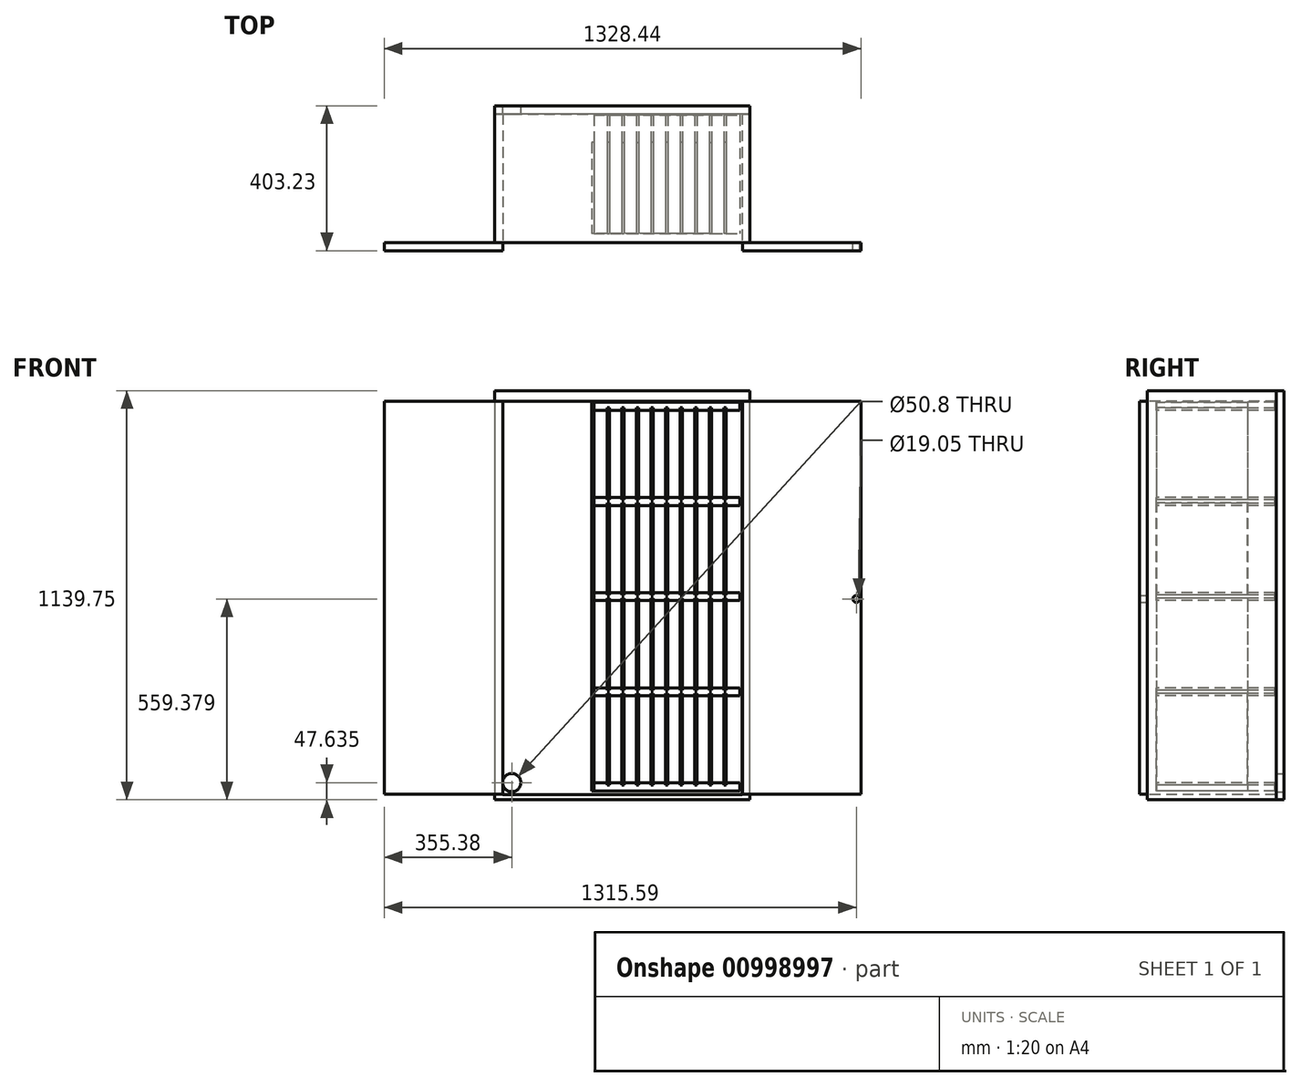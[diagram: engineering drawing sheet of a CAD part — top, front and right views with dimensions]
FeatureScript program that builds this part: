
annotation { "Feature Type Name" : "Feature", "Feature Type Description" : "" }
export const myFeature = defineFeature(function(context is Context, id is Id, definition is map)
    precondition{}
    {
        {
            var Q0;
            Q0=qCreatedBy(makeId("Front.planeOp"),FACE);
            var sketch = newSketch(context, id + "F0", { "sketchPlane" : qUnion([Q0])});
            skLineSegment(sketch, "E0.left", {"start": v(-203.2, -26.35) * mm, "end": v(-203.2, -4.13) * mm});
            skLineSegment(sketch, "E0.right", {"start": v(203.2, -26.35) * mm, "end": v(203.2, -4.13) * mm});
            skPoint(sketch, "E0.middle", {"position": v(0, -15.24) * mm});
            skLineSegment(sketch, "E1", {"start": v(159.39, -10.48) * mm, "end": v(165.74, -10.48) * mm});
            skLineSegment(sketch, "E2", {"start": v(165.74, -20) * mm, "end": v(159.39, -20) * mm});
            skLineSegment(sketch, "E3", {"start": v(165.74, -26.35) * mm, "end": v(165.74, -20) * mm});
            skLineSegment(sketch, "E4", {"start": v(165.74, -10.48) * mm, "end": v(165.74, -4.13) * mm});
            skLineSegment(sketch, "E5", {"start": v(159.39, -4.13) * mm, "end": v(159.39, -10.48) * mm});
            skLineSegment(sketch, "E6", {"start": v(159.39, -20) * mm, "end": v(159.39, -26.35) * mm});
            skLineSegment(sketch, "E7.1.0.2", {"start": v(118.75, -10.48) * mm, "end": v(125.1, -10.48) * mm});
            skLineSegment(sketch, "E7.1.0.3", {"start": v(118.75, -4.13) * mm, "end": v(118.75, -10.48) * mm});
            skLineSegment(sketch, "E7.1.0.4", {"start": v(125.1, -26.35) * mm, "end": v(125.1, -20) * mm});
            skLineSegment(sketch, "E7.1.0.5", {"start": v(125.1, -10.48) * mm, "end": v(125.1, -4.13) * mm});
            skLineSegment(sketch, "E7.1.0.6", {"start": v(125.1, -20) * mm, "end": v(118.75, -20) * mm});
            skLineSegment(sketch, "E7.1.0.7", {"start": v(118.75, -20) * mm, "end": v(118.75, -26.35) * mm});
            skLineSegment(sketch, "E7.2.0.2", {"start": v(78.1, -10.48) * mm, "end": v(84.46, -10.48) * mm});
            skLineSegment(sketch, "E7.2.0.3", {"start": v(78.1, -4.13) * mm, "end": v(78.1, -10.48) * mm});
            skLineSegment(sketch, "E7.2.0.4", {"start": v(84.46, -26.35) * mm, "end": v(84.46, -20) * mm});
            skLineSegment(sketch, "E7.2.0.5", {"start": v(84.46, -10.48) * mm, "end": v(84.46, -4.13) * mm});
            skLineSegment(sketch, "E7.2.0.6", {"start": v(84.46, -20) * mm, "end": v(78.1, -20) * mm});
            skLineSegment(sketch, "E7.2.0.7", {"start": v(78.1, -20) * mm, "end": v(78.1, -26.35) * mm});
            skLineSegment(sketch, "E7.3.0.2", {"start": v(37.47, -10.48) * mm, "end": v(43.82, -10.48) * mm});
            skLineSegment(sketch, "E7.3.0.3", {"start": v(37.47, -4.13) * mm, "end": v(37.47, -10.48) * mm});
            skLineSegment(sketch, "E7.3.0.4", {"start": v(43.82, -26.35) * mm, "end": v(43.82, -20) * mm});
            skLineSegment(sketch, "E7.3.0.5", {"start": v(43.82, -10.48) * mm, "end": v(43.82, -4.13) * mm});
            skLineSegment(sketch, "E7.3.0.6", {"start": v(43.82, -20) * mm, "end": v(37.47, -20) * mm});
            skLineSegment(sketch, "E7.3.0.7", {"start": v(37.47, -20) * mm, "end": v(37.47, -26.35) * mm});
            skLineSegment(sketch, "E7.4.0.2", {"start": v(-3.17, -10.48) * mm, "end": v(3.18, -10.48) * mm});
            skLineSegment(sketch, "E7.4.0.3", {"start": v(-3.17, -4.13) * mm, "end": v(-3.17, -10.48) * mm});
            skLineSegment(sketch, "E7.4.0.4", {"start": v(3.18, -26.35) * mm, "end": v(3.18, -20) * mm});
            skLineSegment(sketch, "E7.4.0.5", {"start": v(3.18, -10.48) * mm, "end": v(3.18, -4.13) * mm});
            skLineSegment(sketch, "E7.4.0.6", {"start": v(3.18, -20) * mm, "end": v(-3.17, -20) * mm});
            skLineSegment(sketch, "E7.4.0.7", {"start": v(-3.17, -20) * mm, "end": v(-3.17, -26.35) * mm});
            skLineSegment(sketch, "E7.5.0.2", {"start": v(-43.81, -10.48) * mm, "end": v(-37.46, -10.48) * mm});
            skLineSegment(sketch, "E7.5.0.3", {"start": v(-43.81, -4.13) * mm, "end": v(-43.81, -10.48) * mm});
            skLineSegment(sketch, "E7.5.0.4", {"start": v(-37.46, -26.35) * mm, "end": v(-37.46, -20) * mm});
            skLineSegment(sketch, "E7.5.0.5", {"start": v(-37.46, -10.48) * mm, "end": v(-37.46, -4.13) * mm});
            skLineSegment(sketch, "E7.5.0.6", {"start": v(-37.46, -20) * mm, "end": v(-43.81, -20) * mm});
            skLineSegment(sketch, "E7.5.0.7", {"start": v(-43.81, -20) * mm, "end": v(-43.81, -26.35) * mm});
            skLineSegment(sketch, "E7.6.0.2", {"start": v(-84.45, -10.48) * mm, "end": v(-78.1, -10.48) * mm});
            skLineSegment(sketch, "E7.6.0.3", {"start": v(-84.45, -4.13) * mm, "end": v(-84.45, -10.48) * mm});
            skLineSegment(sketch, "E7.6.0.4", {"start": v(-78.1, -26.35) * mm, "end": v(-78.1, -20) * mm});
            skLineSegment(sketch, "E7.6.0.5", {"start": v(-78.1, -10.48) * mm, "end": v(-78.1, -4.13) * mm});
            skLineSegment(sketch, "E7.6.0.6", {"start": v(-78.1, -20) * mm, "end": v(-84.45, -20) * mm});
            skLineSegment(sketch, "E7.6.0.7", {"start": v(-84.45, -20) * mm, "end": v(-84.45, -26.35) * mm});
            skLineSegment(sketch, "E7.7.0.2", {"start": v(-125.1, -10.48) * mm, "end": v(-118.74, -10.48) * mm});
            skLineSegment(sketch, "E7.7.0.3", {"start": v(-125.1, -4.13) * mm, "end": v(-125.1, -10.48) * mm});
            skLineSegment(sketch, "E7.7.0.4", {"start": v(-118.74, -26.35) * mm, "end": v(-118.74, -20) * mm});
            skLineSegment(sketch, "E7.7.0.5", {"start": v(-118.74, -10.48) * mm, "end": v(-118.74, -4.13) * mm});
            skLineSegment(sketch, "E7.7.0.6", {"start": v(-118.74, -20) * mm, "end": v(-125.1, -20) * mm});
            skLineSegment(sketch, "E7.7.0.7", {"start": v(-125.1, -20) * mm, "end": v(-125.1, -26.35) * mm});
            skLineSegment(sketch, "E7.8.0.2", {"start": v(-165.73, -10.48) * mm, "end": v(-159.38, -10.48) * mm});
            skLineSegment(sketch, "E7.8.0.3", {"start": v(-165.73, -4.13) * mm, "end": v(-165.73, -10.48) * mm});
            skLineSegment(sketch, "E7.8.0.4", {"start": v(-159.38, -26.35) * mm, "end": v(-159.38, -20) * mm});
            skLineSegment(sketch, "E7.8.0.5", {"start": v(-159.38, -10.48) * mm, "end": v(-159.38, -4.13) * mm});
            skLineSegment(sketch, "E7.8.0.6", {"start": v(-159.38, -20) * mm, "end": v(-165.73, -20) * mm});
            skLineSegment(sketch, "E7.8.0.7", {"start": v(-165.73, -20) * mm, "end": v(-165.73, -26.35) * mm});
            skLineSegment(sketch, "E8.0.2.1", {"start": v(203.2, -556.58) * mm, "end": v(203.2, -534.35) * mm});
            skPoint(sketch, "E8.0.2.3", {"position": v(0, -545.46) * mm});
            skLineSegment(sketch, "E8.0.2.4", {"start": v(-203.2, -556.58) * mm, "end": v(-203.2, -534.35) * mm});
            skLineSegment(sketch, "E8.0.2.8", {"start": v(78.1, -540.7) * mm, "end": v(84.46, -540.7) * mm});
            skLineSegment(sketch, "E8.0.2.11", {"start": v(118.75, -534.35) * mm, "end": v(118.75, -540.7) * mm});
            skLineSegment(sketch, "E8.0.2.14", {"start": v(-165.73, -540.7) * mm, "end": v(-159.38, -540.7) * mm});
            skLineSegment(sketch, "E8.0.2.19", {"start": v(-78.1, -540.7) * mm, "end": v(-78.1, -534.35) * mm});
            skLineSegment(sketch, "E8.0.2.27", {"start": v(-159.38, -540.7) * mm, "end": v(-159.38, -534.35) * mm});
            skLineSegment(sketch, "E8.0.2.31", {"start": v(78.1, -534.35) * mm, "end": v(78.1, -540.7) * mm});
            skLineSegment(sketch, "E8.0.2.33", {"start": v(-84.45, -540.7) * mm, "end": v(-78.1, -540.7) * mm});
            skLineSegment(sketch, "E8.0.2.34", {"start": v(-165.73, -534.35) * mm, "end": v(-165.73, -540.7) * mm});
            skLineSegment(sketch, "E8.0.2.35", {"start": v(84.46, -540.7) * mm, "end": v(84.46, -534.35) * mm});
            skLineSegment(sketch, "E8.0.2.41", {"start": v(-84.45, -534.35) * mm, "end": v(-84.45, -540.7) * mm});
            skLineSegment(sketch, "E8.0.2.46", {"start": v(159.39, -540.7) * mm, "end": v(165.74, -540.7) * mm});
            skLineSegment(sketch, "E8.0.2.47", {"start": v(3.18, -540.7) * mm, "end": v(3.18, -534.35) * mm});
            skLineSegment(sketch, "E8.0.2.48", {"start": v(-125.1, -540.7) * mm, "end": v(-118.74, -540.7) * mm});
            skLineSegment(sketch, "E8.0.2.49", {"start": v(37.47, -534.35) * mm, "end": v(37.47, -540.7) * mm});
            skLineSegment(sketch, "E8.0.2.51", {"start": v(118.75, -540.7) * mm, "end": v(125.1, -540.7) * mm});
            skLineSegment(sketch, "E8.0.2.52", {"start": v(125.1, -540.7) * mm, "end": v(125.1, -534.35) * mm});
            skLineSegment(sketch, "E8.0.2.54", {"start": v(-3.17, -540.7) * mm, "end": v(3.18, -540.7) * mm});
            skLineSegment(sketch, "E8.0.2.55", {"start": v(-37.46, -540.7) * mm, "end": v(-37.46, -534.35) * mm});
            skLineSegment(sketch, "E8.0.2.57", {"start": v(-118.74, -540.7) * mm, "end": v(-118.74, -534.35) * mm});
            skLineSegment(sketch, "E8.0.2.58", {"start": v(-43.81, -534.35) * mm, "end": v(-43.81, -540.7) * mm});
            skLineSegment(sketch, "E8.0.2.62", {"start": v(43.82, -540.7) * mm, "end": v(43.82, -534.35) * mm});
            skLineSegment(sketch, "E8.0.2.63", {"start": v(159.39, -534.35) * mm, "end": v(159.39, -540.7) * mm});
            skLineSegment(sketch, "E8.0.2.65", {"start": v(-125.1, -534.35) * mm, "end": v(-125.1, -540.7) * mm});
            skLineSegment(sketch, "E8.0.2.68", {"start": v(-43.81, -540.7) * mm, "end": v(-37.46, -540.7) * mm});
            skLineSegment(sketch, "E8.0.2.69", {"start": v(165.74, -540.7) * mm, "end": v(165.74, -534.35) * mm});
            skLineSegment(sketch, "E8.0.2.73", {"start": v(-3.17, -534.35) * mm, "end": v(-3.17, -540.7) * mm});
            skLineSegment(sketch, "E8.0.2.75", {"start": v(37.47, -540.7) * mm, "end": v(43.82, -540.7) * mm});
            skLineSegment(sketch, "E9.16.0.2", {"start": v(43.82, 503.87) * mm, "end": v(43.82, 510.22) * mm});
            skLineSegment(sketch, "E9.19.0.2", {"start": v(-125.1, 510.22) * mm, "end": v(-125.1, 503.87) * mm});
            skLineSegment(sketch, "E9.22.0.2", {"start": v(-37.46, 503.87) * mm, "end": v(-37.46, 510.22) * mm});
            skLineSegment(sketch, "E9.25.0.2", {"start": v(-118.74, 503.87) * mm, "end": v(-118.74, 510.22) * mm});
            skLineSegment(sketch, "E9.28.0.2", {"start": v(118.75, 510.22) * mm, "end": v(118.75, 503.87) * mm});
            skLineSegment(sketch, "E9.34.0.2", {"start": v(203.2, 503.87) * mm, "end": v(203.2, 526.1) * mm});
            skLineSegment(sketch, "E9.43.0.2", {"start": v(-43.81, 510.22) * mm, "end": v(-43.81, 503.87) * mm});
            skLineSegment(sketch, "E9.49.0.2", {"start": v(-203.2, 503.87) * mm, "end": v(-203.2, 526.1) * mm});
            skLineSegment(sketch, "E9.55.0.2", {"start": v(37.47, 510.22) * mm, "end": v(37.47, 503.87) * mm});
            skLineSegment(sketch, "E9.76.0.2", {"start": v(78.1, 510.22) * mm, "end": v(78.1, 503.87) * mm});
            skLineSegment(sketch, "E9.91.0.2", {"start": v(165.74, 503.87) * mm, "end": v(165.74, 510.22) * mm});
            skLineSegment(sketch, "E9.100.0.2", {"start": v(-159.38, 503.87) * mm, "end": v(-159.38, 510.22) * mm});
            skLineSegment(sketch, "E9.103.0.2", {"start": v(-37.46, 510.22) * mm, "end": v(-43.81, 510.22) * mm});
            skLineSegment(sketch, "E9.109.0.2", {"start": v(-78.1, 503.87) * mm, "end": v(-78.1, 510.22) * mm});
            skLineSegment(sketch, "E9.112.0.2", {"start": v(43.82, 510.22) * mm, "end": v(37.47, 510.22) * mm});
            skLineSegment(sketch, "E9.118.0.2", {"start": v(84.46, 510.22) * mm, "end": v(78.1, 510.22) * mm});
            skLineSegment(sketch, "E9.124.0.2", {"start": v(-84.45, 510.22) * mm, "end": v(-84.45, 503.87) * mm});
            skLineSegment(sketch, "E9.136.0.2", {"start": v(159.39, 510.22) * mm, "end": v(159.39, 503.87) * mm});
            skLineSegment(sketch, "E9.142.0.2", {"start": v(3.18, 510.22) * mm, "end": v(-3.17, 510.22) * mm});
            skLineSegment(sketch, "E9.145.0.2", {"start": v(-159.38, 510.22) * mm, "end": v(-165.73, 510.22) * mm});
            skLineSegment(sketch, "E9.148.0.2", {"start": v(3.18, 503.87) * mm, "end": v(3.18, 510.22) * mm});
            skLineSegment(sketch, "E9.166.0.2", {"start": v(-118.74, 510.22) * mm, "end": v(-125.1, 510.22) * mm});
            skLineSegment(sketch, "E9.172.0.2", {"start": v(-78.1, 510.22) * mm, "end": v(-84.45, 510.22) * mm});
            skLineSegment(sketch, "E9.178.0.2", {"start": v(-165.73, 510.22) * mm, "end": v(-165.73, 503.87) * mm});
            skLineSegment(sketch, "E9.181.0.2", {"start": v(125.1, 510.22) * mm, "end": v(118.75, 510.22) * mm});
            skLineSegment(sketch, "E9.193.0.2", {"start": v(125.1, 503.87) * mm, "end": v(125.1, 510.22) * mm});
            skLineSegment(sketch, "E9.208.0.2", {"start": v(-3.17, 510.22) * mm, "end": v(-3.17, 503.87) * mm});
            skLineSegment(sketch, "E9.214.0.2", {"start": v(84.46, 503.87) * mm, "end": v(84.46, 510.22) * mm});
            skLineSegment(sketch, "E9.229.0.2", {"start": v(165.74, 510.22) * mm, "end": v(159.39, 510.22) * mm});
            skLineSegment(sketch, "E10", {"start": v(-203.2, -556.58) * mm, "end": v(203.2, -556.58) * mm});
            skLineSegment(sketch, "E11", {"start": v(-203.2, 526.1) * mm, "end": v(203.2, 526.1) * mm});
            skLineSegment(sketch, "E12", {"start": v(203.2, 503.87) * mm, "end": v(165.74, 503.87) * mm});
            skLineSegment(sketch, "E13", {"start": v(118.75, 503.87) * mm, "end": v(84.46, 503.87) * mm});
            skLineSegment(sketch, "E14", {"start": v(78.1, 503.87) * mm, "end": v(43.82, 503.87) * mm});
            skLineSegment(sketch, "E15", {"start": v(37.47, 503.87) * mm, "end": v(3.18, 503.87) * mm});
            skLineSegment(sketch, "E16", {"start": v(-3.17, 503.87) * mm, "end": v(-37.46, 503.87) * mm});
            skLineSegment(sketch, "E17", {"start": v(-43.81, 503.87) * mm, "end": v(-78.1, 503.87) * mm});
            skLineSegment(sketch, "E18", {"start": v(-84.45, 503.87) * mm, "end": v(-118.74, 503.87) * mm});
            skLineSegment(sketch, "E19", {"start": v(-125.1, 503.87) * mm, "end": v(-159.38, 503.87) * mm});
            skLineSegment(sketch, "E20", {"start": v(-165.73, 503.87) * mm, "end": v(-203.2, 503.87) * mm});
            skLineSegment(sketch, "E21", {"start": v(159.39, 503.87) * mm, "end": v(125.1, 503.87) * mm});
            skLineSegment(sketch, "E22", {"start": v(203.2, -4.13) * mm, "end": v(165.74, -4.13) * mm});
            skLineSegment(sketch, "E23", {"start": v(159.39, -4.13) * mm, "end": v(125.1, -4.13) * mm});
            skLineSegment(sketch, "E24", {"start": v(118.75, -4.13) * mm, "end": v(84.46, -4.13) * mm});
            skLineSegment(sketch, "E25", {"start": v(78.1, -4.13) * mm, "end": v(43.82, -4.13) * mm});
            skLineSegment(sketch, "E26", {"start": v(37.47, -4.13) * mm, "end": v(3.18, -4.13) * mm});
            skLineSegment(sketch, "E27", {"start": v(-3.17, -4.13) * mm, "end": v(-37.46, -4.13) * mm});
            skLineSegment(sketch, "E28", {"start": v(-43.81, -4.13) * mm, "end": v(-78.1, -4.13) * mm});
            skLineSegment(sketch, "E29", {"start": v(-84.45, -4.13) * mm, "end": v(-118.74, -4.13) * mm});
            skLineSegment(sketch, "E30", {"start": v(-125.1, -4.13) * mm, "end": v(-159.38, -4.13) * mm});
            skLineSegment(sketch, "E31", {"start": v(-159.38, -26.35) * mm, "end": v(-125.1, -26.35) * mm});
            skLineSegment(sketch, "E32", {"start": v(-118.74, -26.35) * mm, "end": v(-84.45, -26.35) * mm});
            skLineSegment(sketch, "E33", {"start": v(-78.1, -26.35) * mm, "end": v(-43.81, -26.35) * mm});
            skLineSegment(sketch, "E34", {"start": v(-37.46, -26.35) * mm, "end": v(-3.17, -26.35) * mm});
            skLineSegment(sketch, "E35", {"start": v(3.18, -26.35) * mm, "end": v(37.47, -26.35) * mm});
            skLineSegment(sketch, "E36", {"start": v(43.82, -26.35) * mm, "end": v(78.1, -26.35) * mm});
            skLineSegment(sketch, "E37", {"start": v(84.46, -26.35) * mm, "end": v(118.75, -26.35) * mm});
            skLineSegment(sketch, "E38", {"start": v(125.1, -26.35) * mm, "end": v(159.39, -26.35) * mm});
            skLineSegment(sketch, "E39", {"start": v(165.74, -26.35) * mm, "end": v(203.2, -26.35) * mm});
            skLineSegment(sketch, "E40", {"start": v(-165.73, -4.13) * mm, "end": v(-203.2, -4.13) * mm});
            skLineSegment(sketch, "E41", {"start": v(-203.2, -26.35) * mm, "end": v(-165.73, -26.35) * mm});
            skLineSegment(sketch, "E42", {"start": v(203.2, -534.35) * mm, "end": v(165.74, -534.35) * mm});
            skLineSegment(sketch, "E43", {"start": v(159.39, -534.35) * mm, "end": v(125.1, -534.35) * mm});
            skLineSegment(sketch, "E44", {"start": v(118.75, -534.35) * mm, "end": v(84.46, -534.35) * mm});
            skLineSegment(sketch, "E45", {"start": v(78.1, -534.35) * mm, "end": v(43.82, -534.35) * mm});
            skLineSegment(sketch, "E46", {"start": v(37.47, -534.35) * mm, "end": v(3.18, -534.35) * mm});
            skLineSegment(sketch, "E47", {"start": v(-3.17, -534.35) * mm, "end": v(-37.46, -534.35) * mm});
            skLineSegment(sketch, "E48", {"start": v(-43.81, -534.35) * mm, "end": v(-78.1, -534.35) * mm});
            skLineSegment(sketch, "E49", {"start": v(-84.45, -534.35) * mm, "end": v(-118.74, -534.35) * mm});
            skLineSegment(sketch, "E50", {"start": v(-125.1, -534.35) * mm, "end": v(-159.38, -534.35) * mm});
            skLineSegment(sketch, "E51", {"start": v(-165.73, -534.35) * mm, "end": v(-203.2, -534.35) * mm});
            skLineSegment(sketch, "E52.direction1", {"start": v(-203.2, -26.35) * mm, "end": v(-177.8, -26.35) * mm, "construction": true});
            skLineSegment(sketch, "E53.0.0.1", {"start": v(-203.2, 238.76) * mm, "end": v(-165.73, 238.76) * mm});
            skPoint(sketch, "E53.3.0.1", {"position": v(0, 249.87) * mm});
            skLineSegment(sketch, "E53.4.0.1", {"start": v(-165.73, 260.99) * mm, "end": v(-203.2, 260.99) * mm});
            skLineSegment(sketch, "E53.7.0.1", {"start": v(-159.38, 238.76) * mm, "end": v(-125.1, 238.76) * mm});
            skLineSegment(sketch, "E53.10.0.1", {"start": v(-3.17, 260.99) * mm, "end": v(-37.46, 260.99) * mm});
            skLineSegment(sketch, "E53.13.0.1", {"start": v(-78.1, 238.76) * mm, "end": v(-43.81, 238.76) * mm});
            skLineSegment(sketch, "E53.16.0.1", {"start": v(37.47, 260.99) * mm, "end": v(3.18, 260.99) * mm});
            skLineSegment(sketch, "E53.19.0.1", {"start": v(-37.46, 238.76) * mm, "end": v(-3.17, 238.76) * mm});
            skLineSegment(sketch, "E53.22.0.1", {"start": v(-203.2, 238.76) * mm, "end": v(-203.2, 260.99) * mm});
            skLineSegment(sketch, "E53.25.0.1", {"start": v(203.2, 238.76) * mm, "end": v(203.2, 260.99) * mm});
            skLineSegment(sketch, "E53.28.0.1", {"start": v(-125.1, 260.99) * mm, "end": v(-159.38, 260.99) * mm});
            skLineSegment(sketch, "E53.31.0.1", {"start": v(203.2, 260.99) * mm, "end": v(165.74, 260.99) * mm});
            skLineSegment(sketch, "E53.34.0.1", {"start": v(165.74, 238.76) * mm, "end": v(203.2, 238.76) * mm});
            skLineSegment(sketch, "E53.37.0.1", {"start": v(43.82, 238.76) * mm, "end": v(78.1, 238.76) * mm});
            skLineSegment(sketch, "E53.40.0.1", {"start": v(125.1, 238.76) * mm, "end": v(159.39, 238.76) * mm});
            skLineSegment(sketch, "E53.43.0.1", {"start": v(-43.81, 260.99) * mm, "end": v(-43.81, 254.64) * mm});
            skLineSegment(sketch, "E53.46.0.1", {"start": v(-43.81, 260.99) * mm, "end": v(-78.1, 260.99) * mm});
            skLineSegment(sketch, "E53.49.0.1", {"start": v(165.74, 238.76) * mm, "end": v(165.74, 245.11) * mm});
            skLineSegment(sketch, "E53.52.0.1", {"start": v(-159.38, 238.76) * mm, "end": v(-159.38, 245.11) * mm});
            skLineSegment(sketch, "E53.55.0.1", {"start": v(37.47, 260.99) * mm, "end": v(37.47, 254.64) * mm});
            skLineSegment(sketch, "E53.58.0.1", {"start": v(-43.81, 245.11) * mm, "end": v(-43.81, 238.76) * mm});
            skLineSegment(sketch, "E53.61.0.1", {"start": v(125.1, 245.11) * mm, "end": v(118.75, 245.11) * mm});
            skLineSegment(sketch, "E53.64.0.1", {"start": v(-125.1, 245.11) * mm, "end": v(-125.1, 238.76) * mm});
            skLineSegment(sketch, "E53.67.0.1", {"start": v(-118.74, 238.76) * mm, "end": v(-84.45, 238.76) * mm});
            skLineSegment(sketch, "E53.70.0.1", {"start": v(-125.1, 260.99) * mm, "end": v(-125.1, 254.64) * mm});
            skLineSegment(sketch, "E53.73.0.1", {"start": v(-118.74, 238.76) * mm, "end": v(-118.74, 245.11) * mm});
            skLineSegment(sketch, "E53.76.0.1", {"start": v(-165.73, 245.11) * mm, "end": v(-165.73, 238.76) * mm});
            skLineSegment(sketch, "E53.79.0.1", {"start": v(78.1, 245.11) * mm, "end": v(78.1, 238.76) * mm});
            skLineSegment(sketch, "E53.82.0.1", {"start": v(125.1, 238.76) * mm, "end": v(125.1, 245.11) * mm});
            skLineSegment(sketch, "E53.85.0.1", {"start": v(84.46, 238.76) * mm, "end": v(118.75, 238.76) * mm});
            skLineSegment(sketch, "E53.88.0.1", {"start": v(3.18, 245.11) * mm, "end": v(-3.17, 245.11) * mm});
            skLineSegment(sketch, "E53.91.0.1", {"start": v(-84.45, 260.99) * mm, "end": v(-118.74, 260.99) * mm});
            skLineSegment(sketch, "E53.94.0.1", {"start": v(84.46, 254.64) * mm, "end": v(84.46, 260.99) * mm});
            skLineSegment(sketch, "E53.97.0.1", {"start": v(165.74, 254.64) * mm, "end": v(165.74, 260.99) * mm});
            skLineSegment(sketch, "E53.100.0.1", {"start": v(-3.17, 245.11) * mm, "end": v(-3.17, 238.76) * mm});
            skLineSegment(sketch, "E53.103.0.1", {"start": v(-118.74, 245.11) * mm, "end": v(-125.1, 245.11) * mm});
            skLineSegment(sketch, "E53.106.0.1", {"start": v(43.82, 238.76) * mm, "end": v(43.82, 245.11) * mm});
            skLineSegment(sketch, "E53.109.0.1", {"start": v(-37.46, 245.11) * mm, "end": v(-43.81, 245.11) * mm});
            skLineSegment(sketch, "E53.112.0.1", {"start": v(118.75, 260.99) * mm, "end": v(84.46, 260.99) * mm});
            skLineSegment(sketch, "E53.115.0.1", {"start": v(159.39, 260.99) * mm, "end": v(159.39, 254.64) * mm});
            skLineSegment(sketch, "E53.118.0.1", {"start": v(3.18, 254.64) * mm, "end": v(3.18, 260.99) * mm});
            skLineSegment(sketch, "E53.121.0.1", {"start": v(-159.38, 254.64) * mm, "end": v(-159.38, 260.99) * mm});
            skLineSegment(sketch, "E53.124.0.1", {"start": v(3.18, 238.76) * mm, "end": v(37.47, 238.76) * mm});
            skLineSegment(sketch, "E53.127.0.1", {"start": v(-3.17, 260.99) * mm, "end": v(-3.17, 254.64) * mm});
            skLineSegment(sketch, "E53.130.0.1", {"start": v(-78.1, 254.64) * mm, "end": v(-78.1, 260.99) * mm});
            skLineSegment(sketch, "E53.133.0.1", {"start": v(78.1, 254.64) * mm, "end": v(84.46, 254.64) * mm});
            skLineSegment(sketch, "E53.136.0.1", {"start": v(-125.1, 254.64) * mm, "end": v(-118.74, 254.64) * mm});
            skLineSegment(sketch, "E53.139.0.1", {"start": v(3.18, 238.76) * mm, "end": v(3.18, 245.11) * mm});
            skLineSegment(sketch, "E53.142.0.1", {"start": v(84.46, 238.76) * mm, "end": v(84.46, 245.11) * mm});
            skLineSegment(sketch, "E53.145.0.1", {"start": v(159.39, 260.99) * mm, "end": v(125.1, 260.99) * mm});
            skLineSegment(sketch, "E53.148.0.1", {"start": v(37.47, 254.64) * mm, "end": v(43.82, 254.64) * mm});
            skLineSegment(sketch, "E53.151.0.1", {"start": v(-43.81, 254.64) * mm, "end": v(-37.46, 254.64) * mm});
            skLineSegment(sketch, "E53.154.0.1", {"start": v(43.82, 245.11) * mm, "end": v(37.47, 245.11) * mm});
            skLineSegment(sketch, "E53.157.0.1", {"start": v(125.1, 254.64) * mm, "end": v(125.1, 260.99) * mm});
            skLineSegment(sketch, "E53.160.0.1", {"start": v(-37.46, 254.64) * mm, "end": v(-37.46, 260.99) * mm});
            skLineSegment(sketch, "E53.163.0.1", {"start": v(118.75, 260.99) * mm, "end": v(118.75, 254.64) * mm});
            skLineSegment(sketch, "E53.166.0.1", {"start": v(78.1, 260.99) * mm, "end": v(43.82, 260.99) * mm});
            skLineSegment(sketch, "E53.169.0.1", {"start": v(-165.73, 260.99) * mm, "end": v(-165.73, 254.64) * mm});
            skLineSegment(sketch, "E53.172.0.1", {"start": v(159.39, 245.11) * mm, "end": v(159.39, 238.76) * mm});
            skLineSegment(sketch, "E53.175.0.1", {"start": v(-37.46, 238.76) * mm, "end": v(-37.46, 245.11) * mm});
            skLineSegment(sketch, "E53.178.0.1", {"start": v(165.74, 245.11) * mm, "end": v(159.39, 245.11) * mm});
            skLineSegment(sketch, "E53.181.0.1", {"start": v(84.46, 245.11) * mm, "end": v(78.1, 245.11) * mm});
            skLineSegment(sketch, "E53.184.0.1", {"start": v(118.75, 245.11) * mm, "end": v(118.75, 238.76) * mm});
            skLineSegment(sketch, "E53.187.0.1", {"start": v(43.82, 254.64) * mm, "end": v(43.82, 260.99) * mm});
            skLineSegment(sketch, "E53.190.0.1", {"start": v(-84.45, 260.99) * mm, "end": v(-84.45, 254.64) * mm});
            skLineSegment(sketch, "E53.193.0.1", {"start": v(159.39, 254.64) * mm, "end": v(165.74, 254.64) * mm});
            skLineSegment(sketch, "E53.196.0.1", {"start": v(-159.38, 245.11) * mm, "end": v(-165.73, 245.11) * mm});
            skLineSegment(sketch, "E53.199.0.1", {"start": v(-3.17, 254.64) * mm, "end": v(3.18, 254.64) * mm});
            skLineSegment(sketch, "E53.202.0.1", {"start": v(-84.45, 254.64) * mm, "end": v(-78.1, 254.64) * mm});
            skLineSegment(sketch, "E53.205.0.1", {"start": v(-84.45, 245.11) * mm, "end": v(-84.45, 238.76) * mm});
            skLineSegment(sketch, "E53.208.0.1", {"start": v(118.75, 254.64) * mm, "end": v(125.1, 254.64) * mm});
            skLineSegment(sketch, "E53.211.0.1", {"start": v(-78.1, 238.76) * mm, "end": v(-78.1, 245.11) * mm});
            skLineSegment(sketch, "E53.214.0.1", {"start": v(-165.73, 254.64) * mm, "end": v(-159.38, 254.64) * mm});
            skLineSegment(sketch, "E53.217.0.1", {"start": v(37.47, 245.11) * mm, "end": v(37.47, 238.76) * mm});
            skLineSegment(sketch, "E53.220.0.1", {"start": v(-118.74, 254.64) * mm, "end": v(-118.74, 260.99) * mm});
            skLineSegment(sketch, "E53.223.0.1", {"start": v(78.1, 260.99) * mm, "end": v(78.1, 254.64) * mm});
            skLineSegment(sketch, "E53.226.0.1", {"start": v(-78.1, 245.11) * mm, "end": v(-84.45, 245.11) * mm});
            skLineSegment(sketch, "E54.0.1.0", {"start": v(118.75, -269.24) * mm, "end": v(84.46, -269.24) * mm});
            skLineSegment(sketch, "E54.0.1.1", {"start": v(-43.81, -269.24) * mm, "end": v(-78.1, -269.24) * mm});
            skLineSegment(sketch, "E54.0.1.2", {"start": v(-118.74, -291.46) * mm, "end": v(-84.45, -291.46) * mm});
            skLineSegment(sketch, "E54.0.1.3", {"start": v(-37.46, -291.46) * mm, "end": v(-3.17, -291.46) * mm});
            skLineSegment(sketch, "E54.0.1.4", {"start": v(-84.45, -269.24) * mm, "end": v(-118.74, -269.24) * mm});
            skLineSegment(sketch, "E54.0.1.5", {"start": v(159.39, -269.24) * mm, "end": v(125.1, -269.24) * mm});
            skLineSegment(sketch, "E54.0.1.6", {"start": v(43.82, -291.46) * mm, "end": v(78.1, -291.46) * mm});
            skLineSegment(sketch, "E54.0.1.7", {"start": v(84.46, -291.46) * mm, "end": v(118.75, -291.46) * mm});
            skLineSegment(sketch, "E54.0.1.8", {"start": v(125.1, -291.46) * mm, "end": v(159.39, -291.46) * mm});
            skLineSegment(sketch, "E54.0.1.9", {"start": v(-165.73, -269.24) * mm, "end": v(-203.2, -269.24) * mm});
            skLineSegment(sketch, "E54.0.1.10", {"start": v(203.2, -269.24) * mm, "end": v(165.74, -269.24) * mm});
            skLineSegment(sketch, "E54.0.1.11", {"start": v(-203.2, -291.46) * mm, "end": v(-177.8, -291.46) * mm, "construction": true});
            skLineSegment(sketch, "E54.0.1.12", {"start": v(78.1, -269.24) * mm, "end": v(43.82, -269.24) * mm});
            skLineSegment(sketch, "E54.0.1.13", {"start": v(-78.1, -291.46) * mm, "end": v(-43.81, -291.46) * mm});
            skLineSegment(sketch, "E54.0.1.14", {"start": v(3.18, -291.46) * mm, "end": v(37.47, -291.46) * mm});
            skLineSegment(sketch, "E54.0.1.15", {"start": v(-3.17, -269.24) * mm, "end": v(-37.46, -269.24) * mm});
            skLineSegment(sketch, "E54.0.1.16", {"start": v(-159.38, -291.46) * mm, "end": v(-125.1, -291.46) * mm});
            skPoint(sketch, "E54.0.1.17", {"position": v(0, -280.35) * mm});
            skLineSegment(sketch, "E54.0.1.18", {"start": v(-125.1, -269.24) * mm, "end": v(-159.38, -269.24) * mm});
            skLineSegment(sketch, "E54.0.1.19", {"start": v(37.47, -269.24) * mm, "end": v(3.18, -269.24) * mm});
            skLineSegment(sketch, "E54.0.1.20", {"start": v(165.74, -291.46) * mm, "end": v(203.2, -291.46) * mm});
            skLineSegment(sketch, "E54.0.1.21", {"start": v(-203.2, -291.46) * mm, "end": v(-165.73, -291.46) * mm});
            skLineSegment(sketch, "E54.0.1.22", {"start": v(203.2, -291.46) * mm, "end": v(203.2, -269.24) * mm});
            skLineSegment(sketch, "E54.0.1.23", {"start": v(-43.81, -269.24) * mm, "end": v(-43.81, -275.59) * mm});
            skLineSegment(sketch, "E54.0.1.24", {"start": v(-203.2, -291.46) * mm, "end": v(-203.2, -269.24) * mm});
            skLineSegment(sketch, "E54.0.1.25", {"start": v(-37.46, -275.59) * mm, "end": v(-37.46, -269.24) * mm});
            skLineSegment(sketch, "E54.0.1.26", {"start": v(-165.73, -285.11) * mm, "end": v(-165.73, -291.46) * mm});
            skLineSegment(sketch, "E54.0.1.27", {"start": v(43.82, -291.46) * mm, "end": v(43.82, -285.11) * mm});
            skLineSegment(sketch, "E54.0.1.28", {"start": v(3.18, -275.59) * mm, "end": v(3.18, -269.24) * mm});
            skLineSegment(sketch, "E54.0.1.29", {"start": v(-43.81, -275.59) * mm, "end": v(-37.46, -275.59) * mm});
            skLineSegment(sketch, "E54.0.1.30", {"start": v(37.47, -275.59) * mm, "end": v(43.82, -275.59) * mm});
            skLineSegment(sketch, "E54.0.1.31", {"start": v(-165.73, -269.24) * mm, "end": v(-165.73, -275.59) * mm});
            skLineSegment(sketch, "E54.0.1.32", {"start": v(-3.17, -269.24) * mm, "end": v(-3.17, -275.59) * mm});
            skLineSegment(sketch, "E54.0.1.33", {"start": v(165.74, -275.59) * mm, "end": v(165.74, -269.24) * mm});
            skLineSegment(sketch, "E54.0.1.34", {"start": v(-84.45, -269.24) * mm, "end": v(-84.45, -275.59) * mm});
            skLineSegment(sketch, "E54.0.1.35", {"start": v(-37.46, -291.46) * mm, "end": v(-37.46, -285.11) * mm});
            skLineSegment(sketch, "E54.0.1.36", {"start": v(-159.38, -291.46) * mm, "end": v(-159.38, -285.11) * mm});
            skLineSegment(sketch, "E54.0.1.37", {"start": v(118.75, -269.24) * mm, "end": v(118.75, -275.59) * mm});
            skLineSegment(sketch, "E54.0.1.38", {"start": v(-37.46, -285.11) * mm, "end": v(-43.81, -285.11) * mm});
            skLineSegment(sketch, "E54.0.1.39", {"start": v(-159.38, -275.59) * mm, "end": v(-159.38, -269.24) * mm});
            skLineSegment(sketch, "E54.0.1.40", {"start": v(43.82, -275.59) * mm, "end": v(43.82, -269.24) * mm});
            skLineSegment(sketch, "E54.0.1.41", {"start": v(-43.81, -285.11) * mm, "end": v(-43.81, -291.46) * mm});
            skLineSegment(sketch, "E54.0.1.42", {"start": v(-78.1, -275.59) * mm, "end": v(-78.1, -269.24) * mm});
            skLineSegment(sketch, "E54.0.1.43", {"start": v(84.46, -275.59) * mm, "end": v(84.46, -269.24) * mm});
            skLineSegment(sketch, "E54.0.1.44", {"start": v(-3.17, -285.11) * mm, "end": v(-3.17, -291.46) * mm});
            skLineSegment(sketch, "E54.0.1.45", {"start": v(-118.74, -285.11) * mm, "end": v(-125.1, -285.11) * mm});
            skLineSegment(sketch, "E54.0.1.46", {"start": v(-165.73, -275.59) * mm, "end": v(-159.38, -275.59) * mm});
            skLineSegment(sketch, "E54.0.1.47", {"start": v(159.39, -275.59) * mm, "end": v(165.74, -275.59) * mm});
            skLineSegment(sketch, "E54.0.1.48", {"start": v(78.1, -269.24) * mm, "end": v(78.1, -275.59) * mm});
            skLineSegment(sketch, "E54.0.1.49", {"start": v(118.75, -275.59) * mm, "end": v(125.1, -275.59) * mm});
            skLineSegment(sketch, "E54.0.1.50", {"start": v(37.47, -285.11) * mm, "end": v(37.47, -291.46) * mm});
            skLineSegment(sketch, "E54.0.1.51", {"start": v(84.46, -291.46) * mm, "end": v(84.46, -285.11) * mm});
            skLineSegment(sketch, "E54.0.1.52", {"start": v(125.1, -291.46) * mm, "end": v(125.1, -285.11) * mm});
            skLineSegment(sketch, "E54.0.1.53", {"start": v(118.75, -285.11) * mm, "end": v(118.75, -291.46) * mm});
            skLineSegment(sketch, "E54.0.1.54", {"start": v(125.1, -275.59) * mm, "end": v(125.1, -269.24) * mm});
            skLineSegment(sketch, "E54.0.1.55", {"start": v(159.39, -285.11) * mm, "end": v(159.39, -291.46) * mm});
            skLineSegment(sketch, "E54.0.1.56", {"start": v(3.18, -285.11) * mm, "end": v(-3.17, -285.11) * mm});
            skLineSegment(sketch, "E54.0.1.57", {"start": v(165.74, -291.46) * mm, "end": v(165.74, -285.11) * mm});
            skLineSegment(sketch, "E54.0.1.58", {"start": v(84.46, -285.11) * mm, "end": v(78.1, -285.11) * mm});
            skLineSegment(sketch, "E54.0.1.59", {"start": v(-125.1, -269.24) * mm, "end": v(-125.1, -275.59) * mm});
            skLineSegment(sketch, "E54.0.1.60", {"start": v(-159.38, -285.11) * mm, "end": v(-165.73, -285.11) * mm});
            skLineSegment(sketch, "E54.0.1.61", {"start": v(159.39, -269.24) * mm, "end": v(159.39, -275.59) * mm});
            skLineSegment(sketch, "E54.0.1.62", {"start": v(43.82, -285.11) * mm, "end": v(37.47, -285.11) * mm});
            skLineSegment(sketch, "E54.0.1.63", {"start": v(3.18, -291.46) * mm, "end": v(3.18, -285.11) * mm});
            skLineSegment(sketch, "E54.0.1.64", {"start": v(-125.1, -285.11) * mm, "end": v(-125.1, -291.46) * mm});
            skLineSegment(sketch, "E54.0.1.65", {"start": v(165.74, -285.11) * mm, "end": v(159.39, -285.11) * mm});
            skLineSegment(sketch, "E54.0.1.66", {"start": v(-3.17, -275.59) * mm, "end": v(3.18, -275.59) * mm});
            skLineSegment(sketch, "E54.0.1.67", {"start": v(-118.74, -291.46) * mm, "end": v(-118.74, -285.11) * mm});
            skLineSegment(sketch, "E54.0.1.68", {"start": v(37.47, -269.24) * mm, "end": v(37.47, -275.59) * mm});
            skLineSegment(sketch, "E54.0.1.69", {"start": v(78.1, -275.59) * mm, "end": v(84.46, -275.59) * mm});
            skLineSegment(sketch, "E54.0.1.70", {"start": v(125.1, -285.11) * mm, "end": v(118.75, -285.11) * mm});
            skLineSegment(sketch, "E54.0.1.71", {"start": v(-125.1, -275.59) * mm, "end": v(-118.74, -275.59) * mm});
            skLineSegment(sketch, "E54.0.1.72", {"start": v(-118.74, -275.59) * mm, "end": v(-118.74, -269.24) * mm});
            skLineSegment(sketch, "E54.0.1.73", {"start": v(78.1, -285.11) * mm, "end": v(78.1, -291.46) * mm});
            skLineSegment(sketch, "E54.0.1.74", {"start": v(-84.45, -285.11) * mm, "end": v(-84.45, -291.46) * mm});
            skLineSegment(sketch, "E54.0.1.75", {"start": v(-84.45, -275.59) * mm, "end": v(-78.1, -275.59) * mm});
            skLineSegment(sketch, "E54.0.1.76", {"start": v(-78.1, -291.46) * mm, "end": v(-78.1, -285.11) * mm});
            skLineSegment(sketch, "E54.0.1.77", {"start": v(-78.1, -285.11) * mm, "end": v(-84.45, -285.11) * mm});
            skSolve(sketch);
        }
        {
            var Q0;
            Q0=makeQuery(id+"F0.imprint","IMPRINT",FACE,{"disambiguationData":[TD([[makeQuery(id+"F0.imprint","IMPRINT",EDGE,{"derivedFrom":sQuery(id+"F0.wireOp",EDGE,"E9.16.0.2")}),-1.0]])]});
            var Q1;
            Q1=makeQuery(id+"F0.imprint","IMPRINT",FACE,{"disambiguationData":[TD([[makeQuery(id+"F0.imprint","IMPRINT",EDGE,{"derivedFrom":sQuery(id+"F0.wireOp",EDGE,"E53.0.0.1")}),1.0]])]});
            var Q2;
            Q2=makeQuery(id+"F0.imprint","IMPRINT",FACE,{"disambiguationData":[TD([[makeQuery(id+"F0.imprint","IMPRINT",EDGE,{"derivedFrom":sQuery(id+"F0.wireOp",EDGE,"E0.left")}),-1.0]])]});
            var Q3;
            Q3=makeQuery(id+"F0.imprint","IMPRINT",FACE,{"disambiguationData":[TD([[makeQuery(id+"F0.imprint","IMPRINT",EDGE,{"derivedFrom":sQuery(id+"F0.wireOp",EDGE,"E54.0.1.0")}),1.0]])]});
            var Q4;
            Q4=makeQuery(id+"F0.imprint","IMPRINT",FACE,{"disambiguationData":[TD([[makeQuery(id+"F0.imprint","IMPRINT",EDGE,{"derivedFrom":sQuery(id+"F0.wireOp",EDGE,"E8.0.2.1")}),1.0]])]});
            extrude(context, id + "F1", {"entities" : qUnion([Q0, Q1, Q2, Q3, Q4]), "oppositeDirection" : true, "depth" : 330.2 * mm, "offsetDistance" : 25.4 * mm});
        }
        {
            var Q0;
            Q0=qCreatedBy(makeId("Front.planeOp"),FACE);
            var sketch = newSketch(context, id + "F2", { "sketchPlane" : qUnion([Q0])});
            skPoint(sketch, "E55.middle", {"position": v(0, -15.24) * mm});
            skLineSegment(sketch, "E56", {"start": v(159.39, -10.48) * mm, "end": v(165.74, -10.48) * mm});
            skLineSegment(sketch, "E57", {"start": v(165.74, -20) * mm, "end": v(159.39, -20) * mm});
            skLineSegment(sketch, "E58", {"start": v(165.74, -26.35) * mm, "end": v(165.74, -20) * mm});
            skLineSegment(sketch, "E59", {"start": v(165.74, -10.48) * mm, "end": v(165.74, -4.13) * mm});
            skLineSegment(sketch, "E60", {"start": v(159.39, -4.13) * mm, "end": v(159.39, -10.48) * mm});
            skLineSegment(sketch, "E61", {"start": v(159.39, -20) * mm, "end": v(159.39, -26.35) * mm});
            skLineSegment(sketch, "E62.1.0.2", {"start": v(118.75, -10.48) * mm, "end": v(125.1, -10.48) * mm});
            skLineSegment(sketch, "E62.1.0.3", {"start": v(118.75, -4.13) * mm, "end": v(118.75, -10.48) * mm});
            skLineSegment(sketch, "E62.1.0.4", {"start": v(125.1, -26.35) * mm, "end": v(125.1, -20) * mm});
            skLineSegment(sketch, "E62.1.0.5", {"start": v(125.1, -10.48) * mm, "end": v(125.1, -4.13) * mm});
            skLineSegment(sketch, "E62.1.0.6", {"start": v(125.1, -20) * mm, "end": v(118.75, -20) * mm});
            skLineSegment(sketch, "E62.1.0.7", {"start": v(118.75, -20) * mm, "end": v(118.75, -26.35) * mm});
            skLineSegment(sketch, "E62.2.0.2", {"start": v(78.1, -10.48) * mm, "end": v(84.46, -10.48) * mm});
            skLineSegment(sketch, "E62.2.0.3", {"start": v(78.1, -4.13) * mm, "end": v(78.1, -10.48) * mm});
            skLineSegment(sketch, "E62.2.0.4", {"start": v(84.46, -26.35) * mm, "end": v(84.46, -20) * mm});
            skLineSegment(sketch, "E62.2.0.5", {"start": v(84.46, -10.48) * mm, "end": v(84.46, -4.13) * mm});
            skLineSegment(sketch, "E62.2.0.6", {"start": v(84.46, -20) * mm, "end": v(78.1, -20) * mm});
            skLineSegment(sketch, "E62.2.0.7", {"start": v(78.1, -20) * mm, "end": v(78.1, -26.35) * mm});
            skLineSegment(sketch, "E62.3.0.2", {"start": v(37.47, -10.48) * mm, "end": v(43.82, -10.48) * mm});
            skLineSegment(sketch, "E62.3.0.3", {"start": v(37.47, -4.13) * mm, "end": v(37.47, -10.48) * mm});
            skLineSegment(sketch, "E62.3.0.4", {"start": v(43.82, -26.35) * mm, "end": v(43.82, -20) * mm});
            skLineSegment(sketch, "E62.3.0.5", {"start": v(43.82, -10.48) * mm, "end": v(43.82, -4.13) * mm});
            skLineSegment(sketch, "E62.3.0.6", {"start": v(43.82, -20) * mm, "end": v(37.47, -20) * mm});
            skLineSegment(sketch, "E62.3.0.7", {"start": v(37.47, -20) * mm, "end": v(37.47, -26.35) * mm});
            skLineSegment(sketch, "E62.4.0.2", {"start": v(-3.17, -10.48) * mm, "end": v(3.18, -10.48) * mm});
            skLineSegment(sketch, "E62.4.0.3", {"start": v(-3.17, -4.13) * mm, "end": v(-3.17, -10.48) * mm});
            skLineSegment(sketch, "E62.4.0.4", {"start": v(3.18, -26.35) * mm, "end": v(3.18, -20) * mm});
            skLineSegment(sketch, "E62.4.0.5", {"start": v(3.18, -10.48) * mm, "end": v(3.18, -4.13) * mm});
            skLineSegment(sketch, "E62.4.0.6", {"start": v(3.18, -20) * mm, "end": v(-3.17, -20) * mm});
            skLineSegment(sketch, "E62.4.0.7", {"start": v(-3.17, -20) * mm, "end": v(-3.17, -26.35) * mm});
            skLineSegment(sketch, "E62.5.0.2", {"start": v(-43.81, -10.48) * mm, "end": v(-37.46, -10.48) * mm});
            skLineSegment(sketch, "E62.5.0.3", {"start": v(-43.81, -4.13) * mm, "end": v(-43.81, -10.48) * mm});
            skLineSegment(sketch, "E62.5.0.4", {"start": v(-37.46, -26.35) * mm, "end": v(-37.46, -20) * mm});
            skLineSegment(sketch, "E62.5.0.5", {"start": v(-37.46, -10.48) * mm, "end": v(-37.46, -4.13) * mm});
            skLineSegment(sketch, "E62.5.0.6", {"start": v(-37.46, -20) * mm, "end": v(-43.81, -20) * mm});
            skLineSegment(sketch, "E62.5.0.7", {"start": v(-43.81, -20) * mm, "end": v(-43.81, -26.35) * mm});
            skLineSegment(sketch, "E62.6.0.2", {"start": v(-84.45, -10.48) * mm, "end": v(-78.1, -10.48) * mm});
            skLineSegment(sketch, "E62.6.0.3", {"start": v(-84.45, -4.13) * mm, "end": v(-84.45, -10.48) * mm});
            skLineSegment(sketch, "E62.6.0.4", {"start": v(-78.1, -26.35) * mm, "end": v(-78.1, -20) * mm});
            skLineSegment(sketch, "E62.6.0.5", {"start": v(-78.1, -10.48) * mm, "end": v(-78.1, -4.13) * mm});
            skLineSegment(sketch, "E62.6.0.6", {"start": v(-78.1, -20) * mm, "end": v(-84.45, -20) * mm});
            skLineSegment(sketch, "E62.6.0.7", {"start": v(-84.45, -20) * mm, "end": v(-84.45, -26.35) * mm});
            skLineSegment(sketch, "E62.7.0.2", {"start": v(-125.1, -10.48) * mm, "end": v(-118.74, -10.48) * mm});
            skLineSegment(sketch, "E62.7.0.3", {"start": v(-125.1, -4.13) * mm, "end": v(-125.1, -10.48) * mm});
            skLineSegment(sketch, "E62.7.0.4", {"start": v(-118.74, -26.35) * mm, "end": v(-118.74, -20) * mm});
            skLineSegment(sketch, "E62.7.0.5", {"start": v(-118.74, -10.48) * mm, "end": v(-118.74, -4.13) * mm});
            skLineSegment(sketch, "E62.7.0.6", {"start": v(-118.74, -20) * mm, "end": v(-125.1, -20) * mm});
            skLineSegment(sketch, "E62.7.0.7", {"start": v(-125.1, -20) * mm, "end": v(-125.1, -26.35) * mm});
            skLineSegment(sketch, "E62.8.0.2", {"start": v(-165.73, -10.48) * mm, "end": v(-159.38, -10.48) * mm});
            skLineSegment(sketch, "E62.8.0.3", {"start": v(-165.73, -4.13) * mm, "end": v(-165.73, -10.48) * mm});
            skLineSegment(sketch, "E62.8.0.4", {"start": v(-159.38, -26.35) * mm, "end": v(-159.38, -20) * mm});
            skLineSegment(sketch, "E62.8.0.5", {"start": v(-159.38, -10.48) * mm, "end": v(-159.38, -4.13) * mm});
            skLineSegment(sketch, "E62.8.0.6", {"start": v(-159.38, -20) * mm, "end": v(-165.73, -20) * mm});
            skLineSegment(sketch, "E62.8.0.7", {"start": v(-165.73, -20) * mm, "end": v(-165.73, -26.35) * mm});
            skLineSegment(sketch, "E63.0.2.8", {"start": v(78.1, -540.7) * mm, "end": v(84.46, -540.7) * mm});
            skLineSegment(sketch, "E63.0.2.11", {"start": v(118.75, -534.35) * mm, "end": v(118.75, -540.7) * mm});
            skLineSegment(sketch, "E63.0.2.14", {"start": v(-165.73, -540.7) * mm, "end": v(-159.38, -540.7) * mm});
            skLineSegment(sketch, "E63.0.2.19", {"start": v(-78.1, -540.7) * mm, "end": v(-78.1, -534.35) * mm});
            skLineSegment(sketch, "E63.0.2.27", {"start": v(-159.38, -540.7) * mm, "end": v(-159.38, -534.35) * mm});
            skLineSegment(sketch, "E63.0.2.31", {"start": v(78.1, -534.35) * mm, "end": v(78.1, -540.7) * mm});
            skLineSegment(sketch, "E63.0.2.33", {"start": v(-84.45, -540.7) * mm, "end": v(-78.1, -540.7) * mm});
            skLineSegment(sketch, "E63.0.2.34", {"start": v(-165.73, -534.35) * mm, "end": v(-165.73, -540.7) * mm});
            skLineSegment(sketch, "E63.0.2.35", {"start": v(84.46, -540.7) * mm, "end": v(84.46, -534.35) * mm});
            skLineSegment(sketch, "E63.0.2.41", {"start": v(-84.45, -534.35) * mm, "end": v(-84.45, -540.7) * mm});
            skLineSegment(sketch, "E63.0.2.46", {"start": v(159.39, -540.7) * mm, "end": v(165.74, -540.7) * mm});
            skLineSegment(sketch, "E63.0.2.47", {"start": v(3.18, -540.7) * mm, "end": v(3.18, -534.35) * mm});
            skLineSegment(sketch, "E63.0.2.48", {"start": v(-125.1, -540.7) * mm, "end": v(-118.74, -540.7) * mm});
            skLineSegment(sketch, "E63.0.2.49", {"start": v(37.47, -534.35) * mm, "end": v(37.47, -540.7) * mm});
            skLineSegment(sketch, "E63.0.2.51", {"start": v(118.75, -540.7) * mm, "end": v(125.1, -540.7) * mm});
            skLineSegment(sketch, "E63.0.2.52", {"start": v(125.1, -540.7) * mm, "end": v(125.1, -534.35) * mm});
            skLineSegment(sketch, "E63.0.2.54", {"start": v(-3.17, -540.7) * mm, "end": v(3.18, -540.7) * mm});
            skLineSegment(sketch, "E63.0.2.55", {"start": v(-37.46, -540.7) * mm, "end": v(-37.46, -534.35) * mm});
            skLineSegment(sketch, "E63.0.2.57", {"start": v(-118.74, -540.7) * mm, "end": v(-118.74, -534.35) * mm});
            skLineSegment(sketch, "E63.0.2.58", {"start": v(-43.81, -534.35) * mm, "end": v(-43.81, -540.7) * mm});
            skLineSegment(sketch, "E63.0.2.62", {"start": v(43.82, -540.7) * mm, "end": v(43.82, -534.35) * mm});
            skLineSegment(sketch, "E63.0.2.63", {"start": v(159.39, -534.35) * mm, "end": v(159.39, -540.7) * mm});
            skLineSegment(sketch, "E63.0.2.65", {"start": v(-125.1, -534.35) * mm, "end": v(-125.1, -540.7) * mm});
            skLineSegment(sketch, "E63.0.2.68", {"start": v(-43.81, -540.7) * mm, "end": v(-37.46, -540.7) * mm});
            skLineSegment(sketch, "E63.0.2.69", {"start": v(165.74, -540.7) * mm, "end": v(165.74, -534.35) * mm});
            skLineSegment(sketch, "E63.0.2.73", {"start": v(-3.17, -534.35) * mm, "end": v(-3.17, -540.7) * mm});
            skLineSegment(sketch, "E63.0.2.75", {"start": v(37.47, -540.7) * mm, "end": v(43.82, -540.7) * mm});
            skLineSegment(sketch, "E64.16.0.2", {"start": v(43.82, 503.87) * mm, "end": v(43.82, 510.22) * mm});
            skLineSegment(sketch, "E64.19.0.2", {"start": v(-125.1, 510.22) * mm, "end": v(-125.1, 503.87) * mm});
            skLineSegment(sketch, "E64.22.0.2", {"start": v(-37.46, 503.87) * mm, "end": v(-37.46, 510.22) * mm});
            skLineSegment(sketch, "E64.25.0.2", {"start": v(-118.74, 503.87) * mm, "end": v(-118.74, 510.22) * mm});
            skLineSegment(sketch, "E64.28.0.2", {"start": v(118.75, 510.22) * mm, "end": v(118.75, 503.87) * mm});
            skLineSegment(sketch, "E64.43.0.2", {"start": v(-43.81, 510.22) * mm, "end": v(-43.81, 503.87) * mm});
            skLineSegment(sketch, "E64.55.0.2", {"start": v(37.47, 510.22) * mm, "end": v(37.47, 503.87) * mm});
            skLineSegment(sketch, "E64.76.0.2", {"start": v(78.1, 510.22) * mm, "end": v(78.1, 503.87) * mm});
            skLineSegment(sketch, "E64.91.0.2", {"start": v(165.74, 503.87) * mm, "end": v(165.74, 510.22) * mm});
            skLineSegment(sketch, "E64.100.0.2", {"start": v(-159.38, 503.87) * mm, "end": v(-159.38, 510.22) * mm});
            skLineSegment(sketch, "E64.103.0.2", {"start": v(-37.46, 510.22) * mm, "end": v(-43.81, 510.22) * mm});
            skLineSegment(sketch, "E64.109.0.2", {"start": v(-78.1, 503.87) * mm, "end": v(-78.1, 510.22) * mm});
            skLineSegment(sketch, "E64.112.0.2", {"start": v(43.82, 510.22) * mm, "end": v(37.47, 510.22) * mm});
            skLineSegment(sketch, "E64.118.0.2", {"start": v(84.46, 510.22) * mm, "end": v(78.1, 510.22) * mm});
            skLineSegment(sketch, "E64.124.0.2", {"start": v(-84.45, 510.22) * mm, "end": v(-84.45, 503.87) * mm});
            skLineSegment(sketch, "E64.136.0.2", {"start": v(159.39, 510.22) * mm, "end": v(159.39, 503.87) * mm});
            skLineSegment(sketch, "E64.142.0.2", {"start": v(3.18, 510.22) * mm, "end": v(-3.17, 510.22) * mm});
            skLineSegment(sketch, "E64.145.0.2", {"start": v(-159.38, 510.22) * mm, "end": v(-165.73, 510.22) * mm});
            skLineSegment(sketch, "E64.148.0.2", {"start": v(3.18, 503.87) * mm, "end": v(3.18, 510.22) * mm});
            skLineSegment(sketch, "E64.166.0.2", {"start": v(-118.74, 510.22) * mm, "end": v(-125.1, 510.22) * mm});
            skLineSegment(sketch, "E64.172.0.2", {"start": v(-78.1, 510.22) * mm, "end": v(-84.45, 510.22) * mm});
            skLineSegment(sketch, "E64.178.0.2", {"start": v(-165.73, 510.22) * mm, "end": v(-165.73, 503.87) * mm});
            skLineSegment(sketch, "E64.181.0.2", {"start": v(125.1, 510.22) * mm, "end": v(118.75, 510.22) * mm});
            skLineSegment(sketch, "E64.193.0.2", {"start": v(125.1, 503.87) * mm, "end": v(125.1, 510.22) * mm});
            skLineSegment(sketch, "E64.208.0.2", {"start": v(-3.17, 510.22) * mm, "end": v(-3.17, 503.87) * mm});
            skLineSegment(sketch, "E64.214.0.2", {"start": v(84.46, 503.87) * mm, "end": v(84.46, 510.22) * mm});
            skLineSegment(sketch, "E64.229.0.2", {"start": v(165.74, 510.22) * mm, "end": v(159.39, 510.22) * mm});
            skPoint(sketch, "E65.3.0.1", {"position": v(1.81, 267.74) * mm});
            skLineSegment(sketch, "E65.43.0.1", {"start": v(-43.81, 260.99) * mm, "end": v(-43.81, 254.64) * mm});
            skLineSegment(sketch, "E65.49.0.1", {"start": v(165.74, 238.76) * mm, "end": v(165.74, 245.11) * mm});
            skLineSegment(sketch, "E65.52.0.1", {"start": v(-159.38, 238.76) * mm, "end": v(-159.38, 245.11) * mm});
            skLineSegment(sketch, "E65.55.0.1", {"start": v(37.47, 260.99) * mm, "end": v(37.47, 254.64) * mm});
            skLineSegment(sketch, "E65.58.0.1", {"start": v(-43.81, 245.11) * mm, "end": v(-43.81, 238.76) * mm});
            skLineSegment(sketch, "E65.61.0.1", {"start": v(125.1, 245.11) * mm, "end": v(118.75, 245.11) * mm});
            skLineSegment(sketch, "E65.64.0.1", {"start": v(-125.1, 245.11) * mm, "end": v(-125.1, 238.76) * mm});
            skLineSegment(sketch, "E65.70.0.1", {"start": v(-125.1, 260.99) * mm, "end": v(-125.1, 254.64) * mm});
            skLineSegment(sketch, "E65.73.0.1", {"start": v(-118.74, 238.76) * mm, "end": v(-118.74, 245.11) * mm});
            skLineSegment(sketch, "E65.76.0.1", {"start": v(-165.73, 245.11) * mm, "end": v(-165.73, 238.76) * mm});
            skLineSegment(sketch, "E65.79.0.1", {"start": v(78.1, 245.11) * mm, "end": v(78.1, 238.76) * mm});
            skLineSegment(sketch, "E65.82.0.1", {"start": v(125.1, 238.76) * mm, "end": v(125.1, 245.11) * mm});
            skLineSegment(sketch, "E65.88.0.1", {"start": v(3.18, 245.11) * mm, "end": v(-3.17, 245.11) * mm});
            skLineSegment(sketch, "E65.94.0.1", {"start": v(84.46, 254.64) * mm, "end": v(84.46, 260.99) * mm});
            skLineSegment(sketch, "E65.97.0.1", {"start": v(165.74, 254.64) * mm, "end": v(165.74, 260.99) * mm});
            skLineSegment(sketch, "E65.100.0.1", {"start": v(-3.17, 245.11) * mm, "end": v(-3.17, 238.76) * mm});
            skLineSegment(sketch, "E65.103.0.1", {"start": v(-118.74, 245.11) * mm, "end": v(-125.1, 245.11) * mm});
            skLineSegment(sketch, "E65.106.0.1", {"start": v(43.82, 238.76) * mm, "end": v(43.82, 245.11) * mm});
            skLineSegment(sketch, "E65.109.0.1", {"start": v(-37.46, 245.11) * mm, "end": v(-43.81, 245.11) * mm});
            skLineSegment(sketch, "E65.115.0.1", {"start": v(159.39, 260.99) * mm, "end": v(159.39, 254.64) * mm});
            skLineSegment(sketch, "E65.118.0.1", {"start": v(3.18, 254.64) * mm, "end": v(3.18, 260.99) * mm});
            skLineSegment(sketch, "E65.121.0.1", {"start": v(-159.38, 254.64) * mm, "end": v(-159.38, 260.99) * mm});
            skLineSegment(sketch, "E65.127.0.1", {"start": v(-3.17, 260.99) * mm, "end": v(-3.17, 254.64) * mm});
            skLineSegment(sketch, "E65.130.0.1", {"start": v(-78.1, 254.64) * mm, "end": v(-78.1, 260.99) * mm});
            skLineSegment(sketch, "E65.133.0.1", {"start": v(78.1, 254.64) * mm, "end": v(84.46, 254.64) * mm});
            skLineSegment(sketch, "E65.136.0.1", {"start": v(-125.1, 254.64) * mm, "end": v(-118.74, 254.64) * mm});
            skLineSegment(sketch, "E65.139.0.1", {"start": v(3.18, 238.76) * mm, "end": v(3.18, 245.11) * mm});
            skLineSegment(sketch, "E65.142.0.1", {"start": v(84.46, 238.76) * mm, "end": v(84.46, 245.11) * mm});
            skLineSegment(sketch, "E65.148.0.1", {"start": v(37.47, 254.64) * mm, "end": v(43.82, 254.64) * mm});
            skLineSegment(sketch, "E65.151.0.1", {"start": v(-43.81, 254.64) * mm, "end": v(-37.46, 254.64) * mm});
            skLineSegment(sketch, "E65.154.0.1", {"start": v(43.82, 245.11) * mm, "end": v(37.47, 245.11) * mm});
            skLineSegment(sketch, "E65.157.0.1", {"start": v(125.1, 254.64) * mm, "end": v(125.1, 260.99) * mm});
            skLineSegment(sketch, "E65.160.0.1", {"start": v(-37.46, 254.64) * mm, "end": v(-37.46, 260.99) * mm});
            skLineSegment(sketch, "E65.163.0.1", {"start": v(118.75, 260.99) * mm, "end": v(118.75, 254.64) * mm});
            skLineSegment(sketch, "E65.169.0.1", {"start": v(-165.73, 260.99) * mm, "end": v(-165.73, 254.64) * mm});
            skLineSegment(sketch, "E65.172.0.1", {"start": v(159.39, 245.11) * mm, "end": v(159.39, 238.76) * mm});
            skLineSegment(sketch, "E65.175.0.1", {"start": v(-37.46, 238.76) * mm, "end": v(-37.46, 245.11) * mm});
            skLineSegment(sketch, "E65.178.0.1", {"start": v(165.74, 245.11) * mm, "end": v(159.39, 245.11) * mm});
            skLineSegment(sketch, "E65.181.0.1", {"start": v(84.46, 245.11) * mm, "end": v(78.1, 245.11) * mm});
            skLineSegment(sketch, "E65.184.0.1", {"start": v(118.75, 245.11) * mm, "end": v(118.75, 238.76) * mm});
            skLineSegment(sketch, "E65.187.0.1", {"start": v(43.82, 254.64) * mm, "end": v(43.82, 260.99) * mm});
            skLineSegment(sketch, "E65.190.0.1", {"start": v(-84.45, 260.99) * mm, "end": v(-84.45, 254.64) * mm});
            skLineSegment(sketch, "E65.193.0.1", {"start": v(159.39, 254.64) * mm, "end": v(165.74, 254.64) * mm});
            skLineSegment(sketch, "E65.196.0.1", {"start": v(-159.38, 245.11) * mm, "end": v(-165.73, 245.11) * mm});
            skLineSegment(sketch, "E65.199.0.1", {"start": v(-3.17, 254.64) * mm, "end": v(3.18, 254.64) * mm});
            skLineSegment(sketch, "E65.202.0.1", {"start": v(-84.45, 254.64) * mm, "end": v(-78.1, 254.64) * mm});
            skLineSegment(sketch, "E65.205.0.1", {"start": v(-84.45, 245.11) * mm, "end": v(-84.45, 238.76) * mm});
            skLineSegment(sketch, "E65.208.0.1", {"start": v(118.75, 254.64) * mm, "end": v(125.1, 254.64) * mm});
            skLineSegment(sketch, "E65.211.0.1", {"start": v(-78.1, 238.76) * mm, "end": v(-78.1, 245.11) * mm});
            skLineSegment(sketch, "E65.214.0.1", {"start": v(-165.73, 254.64) * mm, "end": v(-159.38, 254.64) * mm});
            skLineSegment(sketch, "E65.217.0.1", {"start": v(37.47, 245.11) * mm, "end": v(37.47, 238.76) * mm});
            skLineSegment(sketch, "E65.220.0.1", {"start": v(-118.74, 254.64) * mm, "end": v(-118.74, 260.99) * mm});
            skLineSegment(sketch, "E65.223.0.1", {"start": v(78.1, 260.99) * mm, "end": v(78.1, 254.64) * mm});
            skLineSegment(sketch, "E65.226.0.1", {"start": v(-78.1, 245.11) * mm, "end": v(-84.45, 245.11) * mm});
            skPoint(sketch, "E66.0.1.17", {"position": v(1.81, -262.48) * mm});
            skLineSegment(sketch, "E66.0.1.23", {"start": v(-43.81, -269.24) * mm, "end": v(-43.81, -275.59) * mm});
            skLineSegment(sketch, "E66.0.1.25", {"start": v(-37.46, -275.59) * mm, "end": v(-37.46, -269.24) * mm});
            skLineSegment(sketch, "E66.0.1.26", {"start": v(-165.73, -285.11) * mm, "end": v(-165.73, -291.46) * mm});
            skLineSegment(sketch, "E66.0.1.27", {"start": v(43.82, -291.46) * mm, "end": v(43.82, -285.11) * mm});
            skLineSegment(sketch, "E66.0.1.28", {"start": v(3.18, -275.59) * mm, "end": v(3.18, -269.24) * mm});
            skLineSegment(sketch, "E66.0.1.29", {"start": v(-43.81, -275.59) * mm, "end": v(-37.46, -275.59) * mm});
            skLineSegment(sketch, "E66.0.1.30", {"start": v(37.47, -275.59) * mm, "end": v(43.82, -275.59) * mm});
            skLineSegment(sketch, "E66.0.1.31", {"start": v(-165.73, -269.24) * mm, "end": v(-165.73, -275.59) * mm});
            skLineSegment(sketch, "E66.0.1.32", {"start": v(-3.17, -269.24) * mm, "end": v(-3.17, -275.59) * mm});
            skLineSegment(sketch, "E66.0.1.33", {"start": v(165.74, -275.59) * mm, "end": v(165.74, -269.24) * mm});
            skLineSegment(sketch, "E66.0.1.34", {"start": v(-84.45, -269.24) * mm, "end": v(-84.45, -275.59) * mm});
            skLineSegment(sketch, "E66.0.1.35", {"start": v(-37.46, -291.46) * mm, "end": v(-37.46, -285.11) * mm});
            skLineSegment(sketch, "E66.0.1.36", {"start": v(-159.38, -291.46) * mm, "end": v(-159.38, -285.11) * mm});
            skLineSegment(sketch, "E66.0.1.37", {"start": v(118.75, -269.24) * mm, "end": v(118.75, -275.59) * mm});
            skLineSegment(sketch, "E66.0.1.38", {"start": v(-37.46, -285.11) * mm, "end": v(-43.81, -285.11) * mm});
            skLineSegment(sketch, "E66.0.1.39", {"start": v(-159.38, -275.59) * mm, "end": v(-159.38, -269.24) * mm});
            skLineSegment(sketch, "E66.0.1.40", {"start": v(43.82, -275.59) * mm, "end": v(43.82, -269.24) * mm});
            skLineSegment(sketch, "E66.0.1.41", {"start": v(-43.81, -285.11) * mm, "end": v(-43.81, -291.46) * mm});
            skLineSegment(sketch, "E66.0.1.42", {"start": v(-78.1, -275.59) * mm, "end": v(-78.1, -269.24) * mm});
            skLineSegment(sketch, "E66.0.1.43", {"start": v(84.46, -275.59) * mm, "end": v(84.46, -269.24) * mm});
            skLineSegment(sketch, "E66.0.1.44", {"start": v(-3.17, -285.11) * mm, "end": v(-3.17, -291.46) * mm});
            skLineSegment(sketch, "E66.0.1.45", {"start": v(-118.74, -285.11) * mm, "end": v(-125.1, -285.11) * mm});
            skLineSegment(sketch, "E66.0.1.46", {"start": v(-165.73, -275.59) * mm, "end": v(-159.38, -275.59) * mm});
            skLineSegment(sketch, "E66.0.1.47", {"start": v(159.39, -275.59) * mm, "end": v(165.74, -275.59) * mm});
            skLineSegment(sketch, "E66.0.1.48", {"start": v(78.1, -269.24) * mm, "end": v(78.1, -275.59) * mm});
            skLineSegment(sketch, "E66.0.1.49", {"start": v(118.75, -275.59) * mm, "end": v(125.1, -275.59) * mm});
            skLineSegment(sketch, "E66.0.1.50", {"start": v(37.47, -285.11) * mm, "end": v(37.47, -291.46) * mm});
            skLineSegment(sketch, "E66.0.1.51", {"start": v(84.46, -291.46) * mm, "end": v(84.46, -285.11) * mm});
            skLineSegment(sketch, "E66.0.1.52", {"start": v(125.1, -291.46) * mm, "end": v(125.1, -285.11) * mm});
            skLineSegment(sketch, "E66.0.1.53", {"start": v(118.75, -285.11) * mm, "end": v(118.75, -291.46) * mm});
            skLineSegment(sketch, "E66.0.1.54", {"start": v(125.1, -275.59) * mm, "end": v(125.1, -269.24) * mm});
            skLineSegment(sketch, "E66.0.1.55", {"start": v(159.39, -285.11) * mm, "end": v(159.39, -291.46) * mm});
            skLineSegment(sketch, "E66.0.1.56", {"start": v(3.18, -285.11) * mm, "end": v(-3.17, -285.11) * mm});
            skLineSegment(sketch, "E66.0.1.57", {"start": v(165.74, -291.46) * mm, "end": v(165.74, -285.11) * mm});
            skLineSegment(sketch, "E66.0.1.58", {"start": v(84.46, -285.11) * mm, "end": v(78.1, -285.11) * mm});
            skLineSegment(sketch, "E66.0.1.59", {"start": v(-125.1, -269.24) * mm, "end": v(-125.1, -275.59) * mm});
            skLineSegment(sketch, "E66.0.1.60", {"start": v(-159.38, -285.11) * mm, "end": v(-165.73, -285.11) * mm});
            skLineSegment(sketch, "E66.0.1.61", {"start": v(159.39, -269.24) * mm, "end": v(159.39, -275.59) * mm});
            skLineSegment(sketch, "E66.0.1.62", {"start": v(43.82, -285.11) * mm, "end": v(37.47, -285.11) * mm});
            skLineSegment(sketch, "E66.0.1.63", {"start": v(3.18, -291.46) * mm, "end": v(3.18, -285.11) * mm});
            skLineSegment(sketch, "E66.0.1.64", {"start": v(-125.1, -285.11) * mm, "end": v(-125.1, -291.46) * mm});
            skLineSegment(sketch, "E66.0.1.65", {"start": v(165.74, -285.11) * mm, "end": v(159.39, -285.11) * mm});
            skLineSegment(sketch, "E66.0.1.66", {"start": v(-3.17, -275.59) * mm, "end": v(3.18, -275.59) * mm});
            skLineSegment(sketch, "E66.0.1.67", {"start": v(-118.74, -291.46) * mm, "end": v(-118.74, -285.11) * mm});
            skLineSegment(sketch, "E66.0.1.68", {"start": v(37.47, -269.24) * mm, "end": v(37.47, -275.59) * mm});
            skLineSegment(sketch, "E66.0.1.69", {"start": v(78.1, -275.59) * mm, "end": v(84.46, -275.59) * mm});
            skLineSegment(sketch, "E66.0.1.70", {"start": v(125.1, -285.11) * mm, "end": v(118.75, -285.11) * mm});
            skLineSegment(sketch, "E66.0.1.71", {"start": v(-125.1, -275.59) * mm, "end": v(-118.74, -275.59) * mm});
            skLineSegment(sketch, "E66.0.1.72", {"start": v(-118.74, -275.59) * mm, "end": v(-118.74, -269.24) * mm});
            skLineSegment(sketch, "E66.0.1.73", {"start": v(78.1, -285.11) * mm, "end": v(78.1, -291.46) * mm});
            skLineSegment(sketch, "E66.0.1.74", {"start": v(-84.45, -285.11) * mm, "end": v(-84.45, -291.46) * mm});
            skLineSegment(sketch, "E66.0.1.75", {"start": v(-84.45, -275.59) * mm, "end": v(-78.1, -275.59) * mm});
            skLineSegment(sketch, "E66.0.1.76", {"start": v(-78.1, -291.46) * mm, "end": v(-78.1, -285.11) * mm});
            skLineSegment(sketch, "E66.0.1.77", {"start": v(-78.1, -285.11) * mm, "end": v(-84.45, -285.11) * mm});
            skLineSegment(sketch, "E67", {"start": v(165.74, -291.46) * mm, "end": v(165.74, -534.35) * mm});
            skLineSegment(sketch, "E68", {"start": v(159.39, -291.46) * mm, "end": v(159.39, -534.35) * mm});
            skLineSegment(sketch, "E69.0.1.0", {"start": v(165.74, -26.03) * mm, "end": v(165.74, -268.92) * mm});
            skLineSegment(sketch, "E69.0.1.1", {"start": v(159.39, -26.03) * mm, "end": v(159.39, -268.92) * mm});
            skLineSegment(sketch, "E69.0.1.2", {"start": v(165.74, -26.03) * mm, "end": v(165.74, -19.68) * mm});
            skLineSegment(sketch, "E69.0.1.3", {"start": v(165.74, -19.68) * mm, "end": v(159.39, -19.68) * mm});
            skLineSegment(sketch, "E69.0.1.4", {"start": v(159.39, -19.68) * mm, "end": v(159.39, -26.03) * mm});
            skLineSegment(sketch, "E69.0.1.5", {"start": v(165.74, -275.27) * mm, "end": v(165.74, -268.92) * mm});
            skLineSegment(sketch, "E69.0.1.6", {"start": v(159.39, -268.92) * mm, "end": v(159.39, -275.27) * mm});
            skLineSegment(sketch, "E69.0.1.7", {"start": v(159.39, -275.27) * mm, "end": v(165.74, -275.27) * mm});
            skLineSegment(sketch, "E69.0.2.0", {"start": v(165.74, 239.4) * mm, "end": v(165.74, -3.5) * mm});
            skLineSegment(sketch, "E69.0.2.1", {"start": v(159.39, 239.4) * mm, "end": v(159.39, -3.5) * mm});
            skLineSegment(sketch, "E69.0.2.2", {"start": v(165.74, 239.4) * mm, "end": v(165.74, 245.75) * mm});
            skLineSegment(sketch, "E69.0.2.3", {"start": v(165.74, 245.75) * mm, "end": v(159.39, 245.75) * mm});
            skLineSegment(sketch, "E69.0.2.4", {"start": v(159.39, 245.75) * mm, "end": v(159.39, 239.4) * mm});
            skLineSegment(sketch, "E69.0.2.5", {"start": v(165.74, -9.84) * mm, "end": v(165.74, -3.5) * mm});
            skLineSegment(sketch, "E69.0.2.6", {"start": v(159.39, -3.5) * mm, "end": v(159.39, -9.84) * mm});
            skLineSegment(sketch, "E69.0.2.7", {"start": v(159.39, -9.84) * mm, "end": v(165.74, -9.84) * mm});
            skLineSegment(sketch, "E69.0.3.0", {"start": v(165.74, 504.83) * mm, "end": v(165.74, 261.94) * mm});
            skLineSegment(sketch, "E69.0.3.1", {"start": v(159.39, 504.83) * mm, "end": v(159.39, 261.94) * mm});
            skLineSegment(sketch, "E69.0.3.2", {"start": v(165.74, 504.83) * mm, "end": v(165.74, 511.18) * mm});
            skLineSegment(sketch, "E69.0.3.3", {"start": v(165.74, 511.18) * mm, "end": v(159.39, 511.18) * mm});
            skLineSegment(sketch, "E69.0.3.4", {"start": v(159.39, 511.18) * mm, "end": v(159.39, 504.83) * mm});
            skLineSegment(sketch, "E69.0.3.5", {"start": v(165.74, 255.59) * mm, "end": v(165.74, 261.94) * mm});
            skLineSegment(sketch, "E69.0.3.6", {"start": v(159.39, 261.94) * mm, "end": v(159.39, 255.59) * mm});
            skLineSegment(sketch, "E69.0.3.7", {"start": v(159.39, 255.59) * mm, "end": v(165.74, 255.59) * mm});
            skLineSegment(sketch, "E69.1.0.0", {"start": v(125.1, -291.46) * mm, "end": v(125.1, -534.35) * mm});
            skLineSegment(sketch, "E69.1.0.1", {"start": v(118.75, -291.46) * mm, "end": v(118.75, -534.35) * mm});
            skLineSegment(sketch, "E69.1.1.0", {"start": v(125.1, -26.03) * mm, "end": v(125.1, -268.92) * mm});
            skLineSegment(sketch, "E69.1.1.1", {"start": v(118.75, -26.03) * mm, "end": v(118.75, -268.92) * mm});
            skLineSegment(sketch, "E69.1.1.2", {"start": v(125.1, -26.03) * mm, "end": v(125.1, -19.68) * mm});
            skLineSegment(sketch, "E69.1.1.3", {"start": v(125.1, -19.68) * mm, "end": v(118.75, -19.68) * mm});
            skLineSegment(sketch, "E69.1.1.4", {"start": v(118.75, -19.68) * mm, "end": v(118.75, -26.03) * mm});
            skLineSegment(sketch, "E69.1.1.5", {"start": v(125.1, -275.27) * mm, "end": v(125.1, -268.92) * mm});
            skLineSegment(sketch, "E69.1.1.6", {"start": v(118.75, -268.92) * mm, "end": v(118.75, -275.27) * mm});
            skLineSegment(sketch, "E69.1.1.7", {"start": v(118.75, -275.27) * mm, "end": v(125.1, -275.27) * mm});
            skLineSegment(sketch, "E69.1.2.0", {"start": v(125.1, 239.4) * mm, "end": v(125.1, -3.5) * mm});
            skLineSegment(sketch, "E69.1.2.1", {"start": v(118.75, 239.4) * mm, "end": v(118.75, -3.5) * mm});
            skLineSegment(sketch, "E69.1.2.2", {"start": v(125.1, 239.4) * mm, "end": v(125.1, 245.75) * mm});
            skLineSegment(sketch, "E69.1.2.3", {"start": v(125.1, 245.75) * mm, "end": v(118.75, 245.75) * mm});
            skLineSegment(sketch, "E69.1.2.4", {"start": v(118.75, 245.75) * mm, "end": v(118.75, 239.4) * mm});
            skLineSegment(sketch, "E69.1.2.5", {"start": v(125.1, -9.84) * mm, "end": v(125.1, -3.5) * mm});
            skLineSegment(sketch, "E69.1.2.6", {"start": v(118.75, -3.5) * mm, "end": v(118.75, -9.84) * mm});
            skLineSegment(sketch, "E69.1.2.7", {"start": v(118.75, -9.84) * mm, "end": v(125.1, -9.84) * mm});
            skLineSegment(sketch, "E69.1.3.0", {"start": v(125.1, 504.83) * mm, "end": v(125.1, 261.94) * mm});
            skLineSegment(sketch, "E69.1.3.1", {"start": v(118.75, 504.83) * mm, "end": v(118.75, 261.94) * mm});
            skLineSegment(sketch, "E69.1.3.2", {"start": v(125.1, 504.83) * mm, "end": v(125.1, 511.18) * mm});
            skLineSegment(sketch, "E69.1.3.3", {"start": v(125.1, 511.18) * mm, "end": v(118.75, 511.18) * mm});
            skLineSegment(sketch, "E69.1.3.4", {"start": v(118.75, 511.18) * mm, "end": v(118.75, 504.83) * mm});
            skLineSegment(sketch, "E69.1.3.5", {"start": v(125.1, 255.59) * mm, "end": v(125.1, 261.94) * mm});
            skLineSegment(sketch, "E69.1.3.6", {"start": v(118.75, 261.94) * mm, "end": v(118.75, 255.59) * mm});
            skLineSegment(sketch, "E69.1.3.7", {"start": v(118.75, 255.59) * mm, "end": v(125.1, 255.59) * mm});
            skLineSegment(sketch, "E69.2.0.0", {"start": v(84.46, -291.46) * mm, "end": v(84.46, -534.35) * mm});
            skLineSegment(sketch, "E69.2.0.1", {"start": v(78.1, -291.46) * mm, "end": v(78.1, -534.35) * mm});
            skLineSegment(sketch, "E69.2.1.0", {"start": v(84.46, -26.03) * mm, "end": v(84.46, -268.92) * mm});
            skLineSegment(sketch, "E69.2.1.1", {"start": v(78.1, -26.03) * mm, "end": v(78.1, -268.92) * mm});
            skLineSegment(sketch, "E69.2.1.2", {"start": v(84.46, -26.03) * mm, "end": v(84.46, -19.68) * mm});
            skLineSegment(sketch, "E69.2.1.3", {"start": v(84.46, -19.68) * mm, "end": v(78.1, -19.68) * mm});
            skLineSegment(sketch, "E69.2.1.4", {"start": v(78.1, -19.68) * mm, "end": v(78.1, -26.03) * mm});
            skLineSegment(sketch, "E69.2.1.5", {"start": v(84.46, -275.27) * mm, "end": v(84.46, -268.92) * mm});
            skLineSegment(sketch, "E69.2.1.6", {"start": v(78.1, -268.92) * mm, "end": v(78.1, -275.27) * mm});
            skLineSegment(sketch, "E69.2.1.7", {"start": v(78.1, -275.27) * mm, "end": v(84.46, -275.27) * mm});
            skLineSegment(sketch, "E69.2.2.0", {"start": v(84.46, 239.4) * mm, "end": v(84.46, -3.5) * mm});
            skLineSegment(sketch, "E69.2.2.1", {"start": v(78.1, 239.4) * mm, "end": v(78.1, -3.5) * mm});
            skLineSegment(sketch, "E69.2.2.2", {"start": v(84.46, 239.4) * mm, "end": v(84.46, 245.75) * mm});
            skLineSegment(sketch, "E69.2.2.3", {"start": v(84.46, 245.75) * mm, "end": v(78.1, 245.75) * mm});
            skLineSegment(sketch, "E69.2.2.4", {"start": v(78.1, 245.75) * mm, "end": v(78.1, 239.4) * mm});
            skLineSegment(sketch, "E69.2.2.5", {"start": v(84.46, -9.84) * mm, "end": v(84.46, -3.5) * mm});
            skLineSegment(sketch, "E69.2.2.6", {"start": v(78.1, -3.5) * mm, "end": v(78.1, -9.84) * mm});
            skLineSegment(sketch, "E69.2.2.7", {"start": v(78.1, -9.84) * mm, "end": v(84.46, -9.84) * mm});
            skLineSegment(sketch, "E69.2.3.0", {"start": v(84.46, 504.83) * mm, "end": v(84.46, 261.94) * mm});
            skLineSegment(sketch, "E69.2.3.1", {"start": v(78.1, 504.83) * mm, "end": v(78.1, 261.94) * mm});
            skLineSegment(sketch, "E69.2.3.2", {"start": v(84.46, 504.83) * mm, "end": v(84.46, 511.18) * mm});
            skLineSegment(sketch, "E69.2.3.3", {"start": v(84.46, 511.18) * mm, "end": v(78.1, 511.18) * mm});
            skLineSegment(sketch, "E69.2.3.4", {"start": v(78.1, 511.18) * mm, "end": v(78.1, 504.83) * mm});
            skLineSegment(sketch, "E69.2.3.5", {"start": v(84.46, 255.59) * mm, "end": v(84.46, 261.94) * mm});
            skLineSegment(sketch, "E69.2.3.6", {"start": v(78.1, 261.94) * mm, "end": v(78.1, 255.59) * mm});
            skLineSegment(sketch, "E69.2.3.7", {"start": v(78.1, 255.59) * mm, "end": v(84.46, 255.59) * mm});
            skLineSegment(sketch, "E69.3.0.0", {"start": v(43.82, -291.46) * mm, "end": v(43.82, -534.35) * mm});
            skLineSegment(sketch, "E69.3.0.1", {"start": v(37.47, -291.46) * mm, "end": v(37.47, -534.35) * mm});
            skLineSegment(sketch, "E69.3.1.0", {"start": v(43.82, -26.03) * mm, "end": v(43.82, -268.92) * mm});
            skLineSegment(sketch, "E69.3.1.1", {"start": v(37.47, -26.03) * mm, "end": v(37.47, -268.92) * mm});
            skLineSegment(sketch, "E69.3.1.2", {"start": v(43.82, -26.03) * mm, "end": v(43.82, -19.68) * mm});
            skLineSegment(sketch, "E69.3.1.3", {"start": v(43.82, -19.68) * mm, "end": v(37.47, -19.68) * mm});
            skLineSegment(sketch, "E69.3.1.4", {"start": v(37.47, -19.68) * mm, "end": v(37.47, -26.03) * mm});
            skLineSegment(sketch, "E69.3.1.5", {"start": v(43.82, -275.27) * mm, "end": v(43.82, -268.92) * mm});
            skLineSegment(sketch, "E69.3.1.6", {"start": v(37.47, -268.92) * mm, "end": v(37.47, -275.27) * mm});
            skLineSegment(sketch, "E69.3.1.7", {"start": v(37.47, -275.27) * mm, "end": v(43.82, -275.27) * mm});
            skLineSegment(sketch, "E69.3.2.0", {"start": v(43.82, 239.4) * mm, "end": v(43.82, -3.5) * mm});
            skLineSegment(sketch, "E69.3.2.1", {"start": v(37.47, 239.4) * mm, "end": v(37.47, -3.5) * mm});
            skLineSegment(sketch, "E69.3.2.2", {"start": v(43.82, 239.4) * mm, "end": v(43.82, 245.75) * mm});
            skLineSegment(sketch, "E69.3.2.3", {"start": v(43.82, 245.75) * mm, "end": v(37.47, 245.75) * mm});
            skLineSegment(sketch, "E69.3.2.4", {"start": v(37.47, 245.75) * mm, "end": v(37.47, 239.4) * mm});
            skLineSegment(sketch, "E69.3.2.5", {"start": v(43.82, -9.84) * mm, "end": v(43.82, -3.5) * mm});
            skLineSegment(sketch, "E69.3.2.6", {"start": v(37.47, -3.5) * mm, "end": v(37.47, -9.84) * mm});
            skLineSegment(sketch, "E69.3.2.7", {"start": v(37.47, -9.84) * mm, "end": v(43.82, -9.84) * mm});
            skLineSegment(sketch, "E69.3.3.0", {"start": v(43.82, 504.83) * mm, "end": v(43.82, 261.94) * mm});
            skLineSegment(sketch, "E69.3.3.1", {"start": v(37.47, 504.83) * mm, "end": v(37.47, 261.94) * mm});
            skLineSegment(sketch, "E69.3.3.2", {"start": v(43.82, 504.83) * mm, "end": v(43.82, 511.18) * mm});
            skLineSegment(sketch, "E69.3.3.3", {"start": v(43.82, 511.18) * mm, "end": v(37.47, 511.18) * mm});
            skLineSegment(sketch, "E69.3.3.4", {"start": v(37.47, 511.18) * mm, "end": v(37.47, 504.83) * mm});
            skLineSegment(sketch, "E69.3.3.5", {"start": v(43.82, 255.59) * mm, "end": v(43.82, 261.94) * mm});
            skLineSegment(sketch, "E69.3.3.6", {"start": v(37.47, 261.94) * mm, "end": v(37.47, 255.59) * mm});
            skLineSegment(sketch, "E69.3.3.7", {"start": v(37.47, 255.59) * mm, "end": v(43.82, 255.59) * mm});
            skLineSegment(sketch, "E69.4.0.0", {"start": v(3.18, -291.46) * mm, "end": v(3.18, -534.35) * mm});
            skLineSegment(sketch, "E69.4.0.1", {"start": v(-3.17, -291.46) * mm, "end": v(-3.17, -534.35) * mm});
            skLineSegment(sketch, "E69.4.1.0", {"start": v(3.18, -26.03) * mm, "end": v(3.18, -268.92) * mm});
            skLineSegment(sketch, "E69.4.1.1", {"start": v(-3.17, -26.03) * mm, "end": v(-3.17, -268.92) * mm});
            skLineSegment(sketch, "E69.4.1.2", {"start": v(3.18, -26.03) * mm, "end": v(3.18, -19.68) * mm});
            skLineSegment(sketch, "E69.4.1.3", {"start": v(3.18, -19.68) * mm, "end": v(-3.17, -19.68) * mm});
            skLineSegment(sketch, "E69.4.1.4", {"start": v(-3.17, -19.68) * mm, "end": v(-3.17, -26.03) * mm});
            skLineSegment(sketch, "E69.4.1.5", {"start": v(3.18, -275.27) * mm, "end": v(3.18, -268.92) * mm});
            skLineSegment(sketch, "E69.4.1.6", {"start": v(-3.17, -268.92) * mm, "end": v(-3.17, -275.27) * mm});
            skLineSegment(sketch, "E69.4.1.7", {"start": v(-3.17, -275.27) * mm, "end": v(3.18, -275.27) * mm});
            skLineSegment(sketch, "E69.4.2.0", {"start": v(3.18, 239.4) * mm, "end": v(3.18, -3.5) * mm});
            skLineSegment(sketch, "E69.4.2.1", {"start": v(-3.17, 239.4) * mm, "end": v(-3.17, -3.5) * mm});
            skLineSegment(sketch, "E69.4.2.2", {"start": v(3.18, 239.4) * mm, "end": v(3.18, 245.75) * mm});
            skLineSegment(sketch, "E69.4.2.3", {"start": v(3.18, 245.75) * mm, "end": v(-3.17, 245.75) * mm});
            skLineSegment(sketch, "E69.4.2.4", {"start": v(-3.17, 245.75) * mm, "end": v(-3.17, 239.4) * mm});
            skLineSegment(sketch, "E69.4.2.5", {"start": v(3.18, -9.84) * mm, "end": v(3.18, -3.5) * mm});
            skLineSegment(sketch, "E69.4.2.6", {"start": v(-3.17, -3.5) * mm, "end": v(-3.17, -9.84) * mm});
            skLineSegment(sketch, "E69.4.2.7", {"start": v(-3.17, -9.84) * mm, "end": v(3.18, -9.84) * mm});
            skLineSegment(sketch, "E69.4.3.0", {"start": v(3.18, 504.83) * mm, "end": v(3.18, 261.94) * mm});
            skLineSegment(sketch, "E69.4.3.1", {"start": v(-3.17, 504.83) * mm, "end": v(-3.17, 261.94) * mm});
            skLineSegment(sketch, "E69.4.3.2", {"start": v(3.18, 504.83) * mm, "end": v(3.18, 511.18) * mm});
            skLineSegment(sketch, "E69.4.3.3", {"start": v(3.18, 511.18) * mm, "end": v(-3.17, 511.18) * mm});
            skLineSegment(sketch, "E69.4.3.4", {"start": v(-3.17, 511.18) * mm, "end": v(-3.17, 504.83) * mm});
            skLineSegment(sketch, "E69.4.3.5", {"start": v(3.18, 255.59) * mm, "end": v(3.18, 261.94) * mm});
            skLineSegment(sketch, "E69.4.3.6", {"start": v(-3.17, 261.94) * mm, "end": v(-3.17, 255.59) * mm});
            skLineSegment(sketch, "E69.4.3.7", {"start": v(-3.17, 255.59) * mm, "end": v(3.18, 255.59) * mm});
            skLineSegment(sketch, "E69.5.0.0", {"start": v(-37.46, -291.46) * mm, "end": v(-37.46, -534.35) * mm});
            skLineSegment(sketch, "E69.5.0.1", {"start": v(-43.81, -291.46) * mm, "end": v(-43.81, -534.35) * mm});
            skLineSegment(sketch, "E69.5.1.0", {"start": v(-37.46, -26.03) * mm, "end": v(-37.46, -268.92) * mm});
            skLineSegment(sketch, "E69.5.1.1", {"start": v(-43.81, -26.03) * mm, "end": v(-43.81, -268.92) * mm});
            skLineSegment(sketch, "E69.5.1.2", {"start": v(-37.46, -26.03) * mm, "end": v(-37.46, -19.68) * mm});
            skLineSegment(sketch, "E69.5.1.3", {"start": v(-37.46, -19.68) * mm, "end": v(-43.81, -19.68) * mm});
            skLineSegment(sketch, "E69.5.1.4", {"start": v(-43.81, -19.68) * mm, "end": v(-43.81, -26.03) * mm});
            skLineSegment(sketch, "E69.5.1.5", {"start": v(-37.46, -275.27) * mm, "end": v(-37.46, -268.92) * mm});
            skLineSegment(sketch, "E69.5.1.6", {"start": v(-43.81, -268.92) * mm, "end": v(-43.81, -275.27) * mm});
            skLineSegment(sketch, "E69.5.1.7", {"start": v(-43.81, -275.27) * mm, "end": v(-37.46, -275.27) * mm});
            skLineSegment(sketch, "E69.5.2.0", {"start": v(-37.46, 239.4) * mm, "end": v(-37.46, -3.5) * mm});
            skLineSegment(sketch, "E69.5.2.1", {"start": v(-43.81, 239.4) * mm, "end": v(-43.81, -3.5) * mm});
            skLineSegment(sketch, "E69.5.2.2", {"start": v(-37.46, 239.4) * mm, "end": v(-37.46, 245.75) * mm});
            skLineSegment(sketch, "E69.5.2.3", {"start": v(-37.46, 245.75) * mm, "end": v(-43.81, 245.75) * mm});
            skLineSegment(sketch, "E69.5.2.4", {"start": v(-43.81, 245.75) * mm, "end": v(-43.81, 239.4) * mm});
            skLineSegment(sketch, "E69.5.2.5", {"start": v(-37.46, -9.84) * mm, "end": v(-37.46, -3.5) * mm});
            skLineSegment(sketch, "E69.5.2.6", {"start": v(-43.81, -3.5) * mm, "end": v(-43.81, -9.84) * mm});
            skLineSegment(sketch, "E69.5.2.7", {"start": v(-43.81, -9.84) * mm, "end": v(-37.46, -9.84) * mm});
            skLineSegment(sketch, "E69.5.3.0", {"start": v(-37.46, 504.83) * mm, "end": v(-37.46, 261.94) * mm});
            skLineSegment(sketch, "E69.5.3.1", {"start": v(-43.81, 504.83) * mm, "end": v(-43.81, 261.94) * mm});
            skLineSegment(sketch, "E69.5.3.2", {"start": v(-37.46, 504.83) * mm, "end": v(-37.46, 511.18) * mm});
            skLineSegment(sketch, "E69.5.3.3", {"start": v(-37.46, 511.18) * mm, "end": v(-43.81, 511.18) * mm});
            skLineSegment(sketch, "E69.5.3.4", {"start": v(-43.81, 511.18) * mm, "end": v(-43.81, 504.83) * mm});
            skLineSegment(sketch, "E69.5.3.5", {"start": v(-37.46, 255.59) * mm, "end": v(-37.46, 261.94) * mm});
            skLineSegment(sketch, "E69.5.3.6", {"start": v(-43.81, 261.94) * mm, "end": v(-43.81, 255.59) * mm});
            skLineSegment(sketch, "E69.5.3.7", {"start": v(-43.81, 255.59) * mm, "end": v(-37.46, 255.59) * mm});
            skLineSegment(sketch, "E69.6.0.0", {"start": v(-78.1, -291.46) * mm, "end": v(-78.1, -534.35) * mm});
            skLineSegment(sketch, "E69.6.0.1", {"start": v(-84.45, -291.46) * mm, "end": v(-84.45, -534.35) * mm});
            skLineSegment(sketch, "E69.6.1.0", {"start": v(-78.1, -26.03) * mm, "end": v(-78.1, -268.92) * mm});
            skLineSegment(sketch, "E69.6.1.1", {"start": v(-84.45, -26.03) * mm, "end": v(-84.45, -268.92) * mm});
            skLineSegment(sketch, "E69.6.1.2", {"start": v(-78.1, -26.03) * mm, "end": v(-78.1, -19.68) * mm});
            skLineSegment(sketch, "E69.6.1.3", {"start": v(-78.1, -19.68) * mm, "end": v(-84.45, -19.68) * mm});
            skLineSegment(sketch, "E69.6.1.4", {"start": v(-84.45, -19.68) * mm, "end": v(-84.45, -26.03) * mm});
            skLineSegment(sketch, "E69.6.1.5", {"start": v(-78.1, -275.27) * mm, "end": v(-78.1, -268.92) * mm});
            skLineSegment(sketch, "E69.6.1.6", {"start": v(-84.45, -268.92) * mm, "end": v(-84.45, -275.27) * mm});
            skLineSegment(sketch, "E69.6.1.7", {"start": v(-84.45, -275.27) * mm, "end": v(-78.1, -275.27) * mm});
            skLineSegment(sketch, "E69.6.2.0", {"start": v(-78.1, 239.4) * mm, "end": v(-78.1, -3.5) * mm});
            skLineSegment(sketch, "E69.6.2.1", {"start": v(-84.45, 239.4) * mm, "end": v(-84.45, -3.5) * mm});
            skLineSegment(sketch, "E69.6.2.2", {"start": v(-78.1, 239.4) * mm, "end": v(-78.1, 245.75) * mm});
            skLineSegment(sketch, "E69.6.2.3", {"start": v(-78.1, 245.75) * mm, "end": v(-84.45, 245.75) * mm});
            skLineSegment(sketch, "E69.6.2.4", {"start": v(-84.45, 245.75) * mm, "end": v(-84.45, 239.4) * mm});
            skLineSegment(sketch, "E69.6.2.5", {"start": v(-78.1, -9.84) * mm, "end": v(-78.1, -3.5) * mm});
            skLineSegment(sketch, "E69.6.2.6", {"start": v(-84.45, -3.5) * mm, "end": v(-84.45, -9.84) * mm});
            skLineSegment(sketch, "E69.6.2.7", {"start": v(-84.45, -9.84) * mm, "end": v(-78.1, -9.84) * mm});
            skLineSegment(sketch, "E69.6.3.0", {"start": v(-78.1, 504.83) * mm, "end": v(-78.1, 261.94) * mm});
            skLineSegment(sketch, "E69.6.3.1", {"start": v(-84.45, 504.83) * mm, "end": v(-84.45, 261.94) * mm});
            skLineSegment(sketch, "E69.6.3.2", {"start": v(-78.1, 504.83) * mm, "end": v(-78.1, 511.18) * mm});
            skLineSegment(sketch, "E69.6.3.3", {"start": v(-78.1, 511.18) * mm, "end": v(-84.45, 511.18) * mm});
            skLineSegment(sketch, "E69.6.3.4", {"start": v(-84.45, 511.18) * mm, "end": v(-84.45, 504.83) * mm});
            skLineSegment(sketch, "E69.6.3.5", {"start": v(-78.1, 255.59) * mm, "end": v(-78.1, 261.94) * mm});
            skLineSegment(sketch, "E69.6.3.6", {"start": v(-84.45, 261.94) * mm, "end": v(-84.45, 255.59) * mm});
            skLineSegment(sketch, "E69.6.3.7", {"start": v(-84.45, 255.59) * mm, "end": v(-78.1, 255.59) * mm});
            skLineSegment(sketch, "E69.7.0.0", {"start": v(-118.74, -291.46) * mm, "end": v(-118.74, -534.35) * mm});
            skLineSegment(sketch, "E69.7.0.1", {"start": v(-125.1, -291.46) * mm, "end": v(-125.1, -534.35) * mm});
            skLineSegment(sketch, "E69.7.1.0", {"start": v(-118.74, -26.03) * mm, "end": v(-118.74, -268.92) * mm});
            skLineSegment(sketch, "E69.7.1.1", {"start": v(-125.1, -26.03) * mm, "end": v(-125.1, -268.92) * mm});
            skLineSegment(sketch, "E69.7.1.2", {"start": v(-118.74, -26.03) * mm, "end": v(-118.74, -19.68) * mm});
            skLineSegment(sketch, "E69.7.1.3", {"start": v(-118.74, -19.68) * mm, "end": v(-125.1, -19.68) * mm});
            skLineSegment(sketch, "E69.7.1.4", {"start": v(-125.1, -19.68) * mm, "end": v(-125.1, -26.03) * mm});
            skLineSegment(sketch, "E69.7.1.5", {"start": v(-118.74, -275.27) * mm, "end": v(-118.74, -268.92) * mm});
            skLineSegment(sketch, "E69.7.1.6", {"start": v(-125.1, -268.92) * mm, "end": v(-125.1, -275.27) * mm});
            skLineSegment(sketch, "E69.7.1.7", {"start": v(-125.1, -275.27) * mm, "end": v(-118.74, -275.27) * mm});
            skLineSegment(sketch, "E69.7.2.0", {"start": v(-118.74, 239.4) * mm, "end": v(-118.74, -3.5) * mm});
            skLineSegment(sketch, "E69.7.2.1", {"start": v(-125.1, 239.4) * mm, "end": v(-125.1, -3.5) * mm});
            skLineSegment(sketch, "E69.7.2.2", {"start": v(-118.74, 239.4) * mm, "end": v(-118.74, 245.75) * mm});
            skLineSegment(sketch, "E69.7.2.3", {"start": v(-118.74, 245.75) * mm, "end": v(-125.1, 245.75) * mm});
            skLineSegment(sketch, "E69.7.2.4", {"start": v(-125.1, 245.75) * mm, "end": v(-125.1, 239.4) * mm});
            skLineSegment(sketch, "E69.7.2.5", {"start": v(-118.74, -9.84) * mm, "end": v(-118.74, -3.5) * mm});
            skLineSegment(sketch, "E69.7.2.6", {"start": v(-125.1, -3.5) * mm, "end": v(-125.1, -9.84) * mm});
            skLineSegment(sketch, "E69.7.2.7", {"start": v(-125.1, -9.84) * mm, "end": v(-118.74, -9.84) * mm});
            skLineSegment(sketch, "E69.7.3.0", {"start": v(-118.74, 504.83) * mm, "end": v(-118.74, 261.94) * mm});
            skLineSegment(sketch, "E69.7.3.1", {"start": v(-125.1, 504.83) * mm, "end": v(-125.1, 261.94) * mm});
            skLineSegment(sketch, "E69.7.3.2", {"start": v(-118.74, 504.83) * mm, "end": v(-118.74, 511.18) * mm});
            skLineSegment(sketch, "E69.7.3.3", {"start": v(-118.74, 511.18) * mm, "end": v(-125.1, 511.18) * mm});
            skLineSegment(sketch, "E69.7.3.4", {"start": v(-125.1, 511.18) * mm, "end": v(-125.1, 504.83) * mm});
            skLineSegment(sketch, "E69.7.3.5", {"start": v(-118.74, 255.59) * mm, "end": v(-118.74, 261.94) * mm});
            skLineSegment(sketch, "E69.7.3.6", {"start": v(-125.1, 261.94) * mm, "end": v(-125.1, 255.59) * mm});
            skLineSegment(sketch, "E69.7.3.7", {"start": v(-125.1, 255.59) * mm, "end": v(-118.74, 255.59) * mm});
            skLineSegment(sketch, "E69.8.0.0", {"start": v(-159.38, -291.46) * mm, "end": v(-159.38, -534.35) * mm});
            skLineSegment(sketch, "E69.8.0.1", {"start": v(-165.73, -291.46) * mm, "end": v(-165.73, -534.35) * mm});
            skLineSegment(sketch, "E69.8.1.0", {"start": v(-159.38, -26.03) * mm, "end": v(-159.38, -268.92) * mm});
            skLineSegment(sketch, "E69.8.1.1", {"start": v(-165.73, -26.03) * mm, "end": v(-165.73, -268.92) * mm});
            skLineSegment(sketch, "E69.8.1.2", {"start": v(-159.38, -26.03) * mm, "end": v(-159.38, -19.68) * mm});
            skLineSegment(sketch, "E69.8.1.3", {"start": v(-159.38, -19.68) * mm, "end": v(-165.73, -19.68) * mm});
            skLineSegment(sketch, "E69.8.1.4", {"start": v(-165.73, -19.68) * mm, "end": v(-165.73, -26.03) * mm});
            skLineSegment(sketch, "E69.8.1.5", {"start": v(-159.38, -275.27) * mm, "end": v(-159.38, -268.92) * mm});
            skLineSegment(sketch, "E69.8.1.6", {"start": v(-165.73, -268.92) * mm, "end": v(-165.73, -275.27) * mm});
            skLineSegment(sketch, "E69.8.1.7", {"start": v(-165.73, -275.27) * mm, "end": v(-159.38, -275.27) * mm});
            skLineSegment(sketch, "E69.8.2.0", {"start": v(-159.38, 239.4) * mm, "end": v(-159.38, -3.5) * mm});
            skLineSegment(sketch, "E69.8.2.1", {"start": v(-165.73, 239.4) * mm, "end": v(-165.73, -3.5) * mm});
            skLineSegment(sketch, "E69.8.2.2", {"start": v(-159.38, 239.4) * mm, "end": v(-159.38, 245.75) * mm});
            skLineSegment(sketch, "E69.8.2.3", {"start": v(-159.38, 245.75) * mm, "end": v(-165.73, 245.75) * mm});
            skLineSegment(sketch, "E69.8.2.4", {"start": v(-165.73, 245.75) * mm, "end": v(-165.73, 239.4) * mm});
            skLineSegment(sketch, "E69.8.2.5", {"start": v(-159.38, -9.84) * mm, "end": v(-159.38, -3.5) * mm});
            skLineSegment(sketch, "E69.8.2.6", {"start": v(-165.73, -3.5) * mm, "end": v(-165.73, -9.84) * mm});
            skLineSegment(sketch, "E69.8.2.7", {"start": v(-165.73, -9.84) * mm, "end": v(-159.38, -9.84) * mm});
            skLineSegment(sketch, "E69.8.3.0", {"start": v(-159.38, 504.83) * mm, "end": v(-159.38, 261.94) * mm});
            skLineSegment(sketch, "E69.8.3.1", {"start": v(-165.73, 504.83) * mm, "end": v(-165.73, 261.94) * mm});
            skLineSegment(sketch, "E69.8.3.2", {"start": v(-159.38, 504.83) * mm, "end": v(-159.38, 511.18) * mm});
            skLineSegment(sketch, "E69.8.3.3", {"start": v(-159.38, 511.18) * mm, "end": v(-165.73, 511.18) * mm});
            skLineSegment(sketch, "E69.8.3.4", {"start": v(-165.73, 511.18) * mm, "end": v(-165.73, 504.83) * mm});
            skLineSegment(sketch, "E69.8.3.5", {"start": v(-159.38, 255.59) * mm, "end": v(-159.38, 261.94) * mm});
            skLineSegment(sketch, "E69.8.3.6", {"start": v(-165.73, 261.94) * mm, "end": v(-165.73, 255.59) * mm});
            skLineSegment(sketch, "E69.8.3.7", {"start": v(-165.73, 255.59) * mm, "end": v(-159.38, 255.59) * mm});
            skPoint(sketch, "E70", {"position": v(-203.19, 524.96) * mm});
            skPoint(sketch, "E71", {"position": v(-203.19, -556.61) * mm});
            skLineSegment(sketch, "E72.bottom", {"start": v(-203.19, 524.96) * mm, "end": v(-209.54, 524.96) * mm});
            skLineSegment(sketch, "E72.top", {"start": v(-203.19, -556.61) * mm, "end": v(-209.54, -556.61) * mm});
            skLineSegment(sketch, "E72.left", {"start": v(-203.19, 524.96) * mm, "end": v(-203.19, -556.61) * mm});
            skLineSegment(sketch, "E72.right", {"start": v(-209.54, 524.96) * mm, "end": v(-209.54, -556.61) * mm});
            skSolve(sketch);
        }
        {
            var Q0;
            Q0 = qSketchRegion(id + "F2", true);
            extrude(context, id + "F3", {"entities" : qUnion([Q0]), "oppositeDirection" : true, "depth" : 254 * mm, "offsetDistance" : 25.4 * mm});
        }
        {
            var Q0;
            Q0=qCreatedBy(makeId("Front.planeOp"),FACE);
            var sketch = newSketch(context, id + "F4", { "sketchPlane" : qUnion([Q0])});
            skLineSegment(sketch, "E73.bottom", {"start": v(209.63, -566.44) * mm, "end": v(-457.12, -566.44) * mm});
            skLineSegment(sketch, "E73.top", {"start": v(209.63, 528.84) * mm, "end": v(-457.12, 528.84) * mm});
            skLineSegment(sketch, "E74.0", {"start": v(231.86, 558.64) * mm, "end": v(-479.34, 558.64) * mm});
            skLineSegment(sketch, "E75.0", {"start": v(231.86, -581.08) * mm, "end": v(-479.34, -581.08) * mm});
            skLineSegment(sketch, "E76", {"start": v(-479.34, 558.64) * mm, "end": v(-479.34, -581.08) * mm});
            skLineSegment(sketch, "E77", {"start": v(-457.12, 528.84) * mm, "end": v(-457.12, -566.44) * mm});
            skLineSegment(sketch, "E78", {"start": v(209.63, 528.84) * mm, "end": v(209.63, -566.44) * mm});
            skLineSegment(sketch, "E79", {"start": v(231.86, -581.08) * mm, "end": v(231.86, 558.64) * mm});
            skSolve(sketch);
        }
        {
            var Q0;
            Q0=makeQuery(id+"F4.imprint","IMPRINT",FACE,{"disambiguationData":[TD([[makeQuery(id+"F4.imprint","IMPRINT",EDGE,{"derivedFrom":sQuery(id+"F4.wireOp",EDGE,"E73.bottom")}),1.0]])]});
            extrude(context, id + "F5", {"entities" : qUnion([Q0]), "oppositeDirection" : true, "depth" : 355.6 * mm, "offsetDistance" : 25.4 * mm, "hasSecondDirection" : true, "secondDirectionOppositeDirection" : false, "secondDirectionDepth" : 25.4 * mm});
        }
        {
            var Q0;
            Q0=makeQuery(id+"F5.opExtrude","CAP_FACE",FACE,{"disambiguationData":[OSD([sQuery(id+"F4.wireOp",EDGE,"E73.bottom"),sQuery(id+"F4.wireOp",EDGE,"E73.top"),sQuery(id+"F4.wireOp",EDGE,"E73.left"),sQuery(id+"F4.wireOp",EDGE,"E73.right"),sQuery(id+"F4.wireOp",EDGE,"E74.0"),sQuery(id+"F4.wireOp",EDGE,"fd27da03-2fb2-4175-96d7-ff5d5455aa17.0"),sQuery(id+"F4.wireOp",EDGE,"2eda592c-bfc0-441b-a2c1-ea656dcc7ac0.0"),sQuery(id+"F4.wireOp",EDGE,"E75.0")])],"isStart":false});
            cPlane(context, id + "F6", {"entities" : qUnion([Q0]), "cplaneType" : CPlaneType.OFFSET, "offset" : 0 * mm, "width" : 152.4 * mm, "height" : 152.4 * mm});
        }
        {
            var Q0;
            Q0=qCreatedBy(id+"F6.planeOp",FACE);
            var sketch = newSketch(context, id + "F7", { "sketchPlane" : qUnion([Q0])});
            skLineSegment(sketch, "E80.0", {"start": v(479.33, 558.62) * mm, "end": v(-231.87, 558.62) * mm});
            skLineSegment(sketch, "E81.0", {"start": v(-231.87, -581.1) * mm, "end": v(-231.87, 558.62) * mm});
            skLineSegment(sketch, "E82.0", {"start": v(479.33, -581.1) * mm, "end": v(479.33, 558.62) * mm});
            skLineSegment(sketch, "E83.0", {"start": v(479.33, -581.1) * mm, "end": v(-231.87, -581.1) * mm});
            skPoint(sketch, "E84", {"position": v(457.2, 536.49) * mm});
            skPoint(sketch, "E85", {"position": v(479.33, 558.62) * mm});
            skPoint(sketch, "E86", {"position": v(457.1, -558.88) * mm});
            skLineSegment(sketch, "E87", {"start": v(457.1, -508.08) * mm, "end": v(406.3, -558.88) * mm, "construction": true});
            skLineSegment(sketch, "E88", {"start": v(447.12, -554.36) * mm, "end": v(457.1, -558.88) * mm, "construction": true});
            skLineSegment(sketch, "E89", {"start": v(406.3, -508.08) * mm, "end": v(457.1, -558.88) * mm, "construction": true});
            skCircle(sketch, "E90", {"center": v(431.7, -533.48) * mm, "radius": 25.4 * mm});
            skSolve(sketch);
        }
        {
            var Q0;
            Q0=makeQuery(id+"F7.imprint","IMPRINT",FACE,{"disambiguationData":[TD([[makeQuery(id+"F7.imprint","IMPRINT",EDGE,{"derivedFrom":sQuery(id+"F7.wireOp",EDGE,"E80.0")}),1.0]])]});
            extrude(context, id + "F8", {"entities" : qUnion([Q0]), "operationType" : NewBodyOperationType.ADD, "oppositeDirection" : true, "depth" : 22.22 * mm, "offsetDistance" : 25.4 * mm});
        }
        {
            var Q0;
            Q0=makeQuery(id+"F7.imprint","IMPRINT",FACE,{"disambiguationData":[TD([[makeQuery(id+"F7.imprint","IMPRINT",EDGE,{"derivedFrom":sQuery(id+"F7.wireOp",EDGE,"E90")}),1.0]])]});
            extrude(context, id + "F9", {"entities" : qUnion([Q0]), "operationType" : NewBodyOperationType.REMOVE, "oppositeDirection" : true, "depth" : 25.4 * mm, "offsetDistance" : 25.4 * mm});
        }
        {
            var Q0;
            Q0=makeQuery(id+"F5.opExtrude","CAP_FACE",FACE,{"disambiguationData":[OSD([sQuery(id+"F4.wireOp",EDGE,"E73.bottom"),sQuery(id+"F4.wireOp",EDGE,"E73.top"),sQuery(id+"F4.wireOp",EDGE,"E74.0"),sQuery(id+"F4.wireOp",EDGE,"E75.0"),sQuery(id+"F4.wireOp",EDGE,"E76"),sQuery(id+"F4.wireOp",EDGE,"E77"),sQuery(id+"F4.wireOp",EDGE,"E78"),sQuery(id+"F4.wireOp",EDGE,"E79")])],"isStart":true});
            cPlane(context, id + "F10", {"entities" : qUnion([Q0]), "cplaneType" : CPlaneType.OFFSET, "offset" : 0 * mm, "width" : 152.4 * mm, "height" : 152.4 * mm});
        }
        {
            var Q0;
            Q0=qCreatedBy(id+"F10.planeOp",FACE);
            var sketch = newSketch(context, id + "F11", { "sketchPlane" : qUnion([Q0])});
            skLineSegment(sketch, "E91", {"start": v(-477.44, -582.98) * mm, "end": v(231.73, 558.77) * mm, "construction": true});
            skLineSegment(sketch, "E92", {"start": v(-477.44, 558.77) * mm, "end": v(231.73, -582.98) * mm, "construction": true});
            skPoint(sketch, "E93", {"position": v(-122.86, -12.1) * mm});
            skLineSegment(sketch, "E94", {"start": v(-122.86, -676.95) * mm, "end": v(-122.86, 636.78) * mm, "construction": true});
            skPoint(sketch, "E95", {"position": v(-456.88, 528.8) * mm});
            skLineSegment(sketch, "E96", {"start": v(-456.88, 528.8) * mm, "end": v(-787.08, 528.8) * mm});
            skPoint(sketch, "E97", {"position": v(-456.52, -566.3) * mm});
            skLineSegment(sketch, "E98", {"start": v(-456.52, -566.3) * mm, "end": v(-786.72, -566.3) * mm});
            skLineSegment(sketch, "E99", {"start": v(-786.72, -566.3) * mm, "end": v(-787.08, 528.8) * mm});
            skLineSegment(sketch, "E100.MirrorCS", {"start": v(211.16, 528.8) * mm, "end": v(210.81, -566.3) * mm});
            skLineSegment(sketch, "E101.MirrorCS", {"start": v(211.16, 528.8) * mm, "end": v(541.36, 528.8) * mm});
            skLineSegment(sketch, "E102.MirrorCS", {"start": v(541.01, -566.3) * mm, "end": v(541.36, 528.8) * mm});
            skLineSegment(sketch, "E103.MirrorCS", {"start": v(210.81, -566.3) * mm, "end": v(541.01, -566.3) * mm});
            skCircle(sketch, "E104", {"center": v(528.51, -21.73) * mm, "radius": 9.53 * mm});
            skLineSegment(sketch, "E105", {"start": v(-354.9, -12.1) * mm, "end": v(258.44, -12.1) * mm, "construction": true});
            skLineSegment(sketch, "E106", {"start": v(-456.88, 528.8) * mm, "end": v(-456.52, -566.3) * mm});
            skSolve(sketch);
        }
        {
            var Q0;
            Q0=makeQuery(id+"F11.imprint","IMPRINT",FACE,{"disambiguationData":[TD([[makeQuery(id+"F11.imprint","IMPRINT",EDGE,{"derivedFrom":sQuery(id+"F11.wireOp",EDGE,"E96")}),1.0]])]});
            var Q1;
            Q1=makeQuery(id+"F11.imprint","IMPRINT",FACE,{"disambiguationData":[TD([[makeQuery(id+"F11.imprint","IMPRINT",EDGE,{"derivedFrom":sQuery(id+"F11.wireOp",EDGE,"E100.MirrorCS")}),1.0]])]});
            var Q2;
            {var subQ5=sQuery(id+"F11.wireOp",EDGE,"945d7d3f-2e24-4aa4-a8fb-3bcfb2968ccc0.MirrorCS");Q2=makeQuery(id+"F11.imprint","IMPRINT",FACE,{"disambiguationData":[TD([[makeQuery(id+"F11.imprint","IMPRINT",EDGE,{"derivedFrom":subQ5}),1.0]])]});}
            var Q3;
            Q3=makeQuery(id+"F11.imprint","IMPRINT",FACE,{"disambiguationData":[TD([[makeQuery(id+"F11.imprint","IMPRINT",EDGE,{"derivedFrom":sQuery(id+"F11.wireOp",EDGE,"PqKMKNCi-Sgya-wTwO-OgJu-uYzNobhRPgVU.bottom")}),1.0]])]});
            extrude(context, id + "F12", {"entities" : qUnion([Q0, Q1, Q2, Q3]), "operationType" : NewBodyOperationType.ADD, "depth" : 22.22 * mm, "offsetDistance" : 25.4 * mm});
        }
    });
